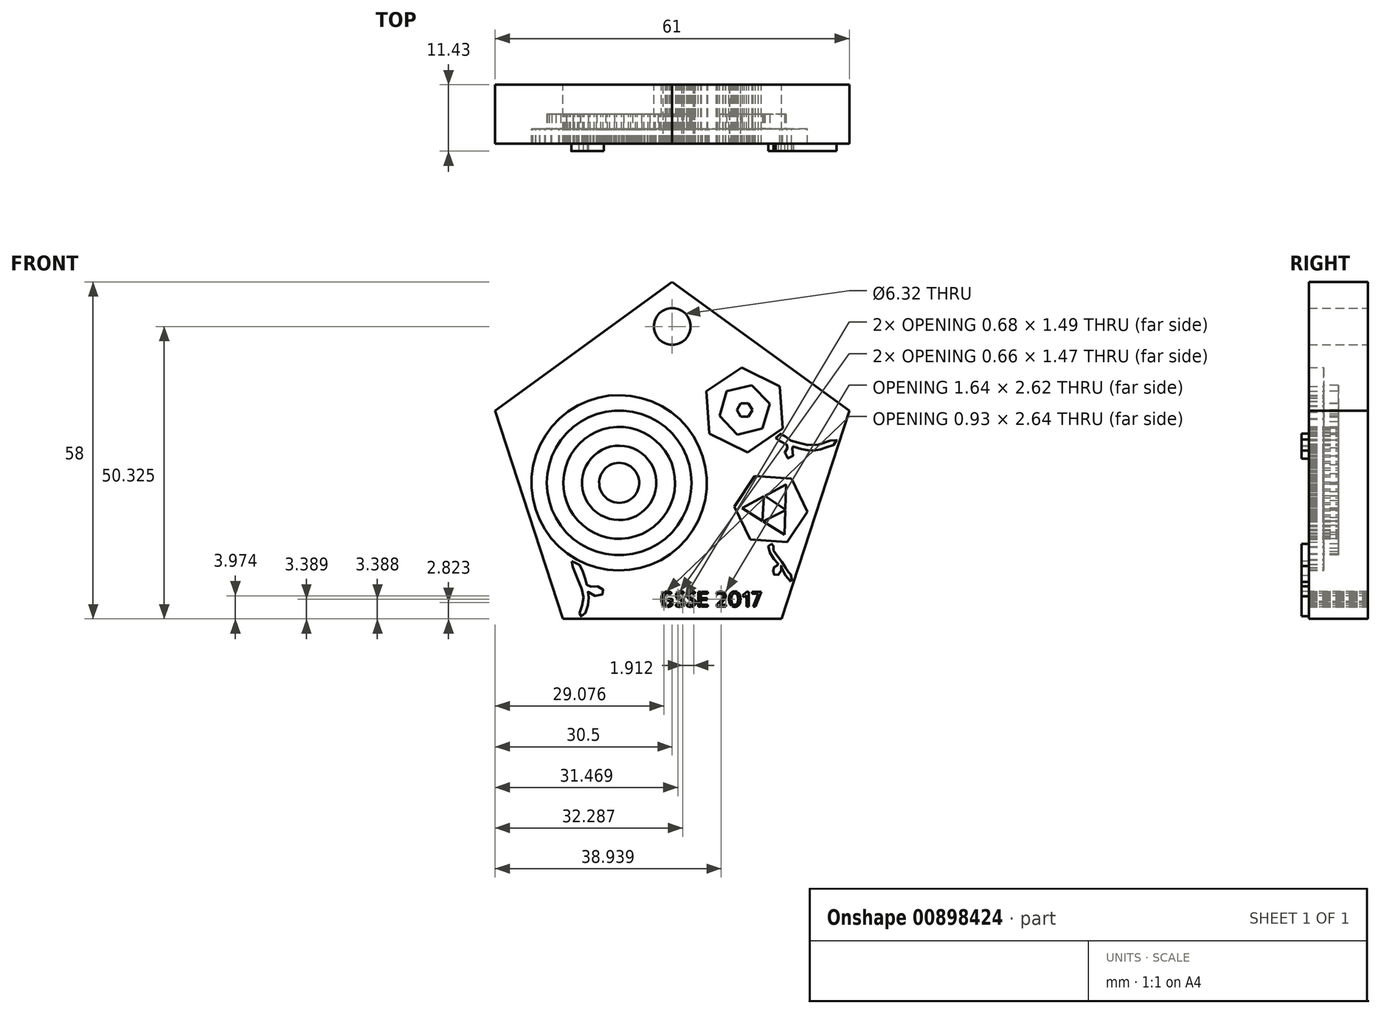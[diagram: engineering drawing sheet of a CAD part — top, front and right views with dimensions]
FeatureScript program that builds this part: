
annotation { "Feature Type Name" : "Feature", "Feature Type Description" : "" }
export const myFeature = defineFeature(function(context is Context, id is Id, definition is map)
    precondition{}
    {
        {
            var Q0;
            Q0=qCreatedBy(makeId("Front.planeOp"),FACE);
            var sketch = newSketch(context, id + "F0", { "sketchPlane" : qUnion([Q0])});
            skCircle(sketch, "E0.cCircle", {"center": v(0, 0) * mm, "radius": 32.06 * mm, "construction": true});
            skLineSegment(sketch, "E0.0", {"start": v(30.5, 9.9) * mm, "end": v(18.85, -25.94) * mm});
            skLineSegment(sketch, "E0.1", {"start": v(18.85, -25.94) * mm, "end": v(-18.85, -25.94) * mm});
            skLineSegment(sketch, "E0.2", {"start": v(-18.85, -25.94) * mm, "end": v(-30.5, 9.9) * mm});
            skLineSegment(sketch, "E0.3", {"start": v(-30.5, 9.9) * mm, "end": v(0, 32.06) * mm});
            skLineSegment(sketch, "E0.4", {"start": v(0, 32.06) * mm, "end": v(30.5, 9.9) * mm});
            skCircle(sketch, "E1", {"center": v(0, 24.38) * mm, "radius": 3.16 * mm});
            skText(sketch, "E2", { "text": "GSSE 2017\n", "fontName": "AllertaStencil-Regular.ttf"});
            const initialGuessF0  = {"E2": [-0.00217, -0.02386, 1, 0, 0.0026]};
            skSetInitialGuess(sketch, initialGuessF0);
            skSolve(sketch);
        }
        {
            var Q0;
            Q0=makeQuery(id+"F0.imprint","IMPRINT",FACE,{"disambiguationData":[TD([[makeQuery(id+"F0.imprint","IMPRINT",EDGE,{"derivedFrom":sQuery(id+"F0.wireOp",EDGE,"E0.0")}),-1.0]])]});
            extrude(context, id + "F1", {"entities" : qUnion([Q0]), "depth" : 7.62 * mm, "offsetDistance" : 25.4 * mm, "symmetric" : true});
        }
        {
            var Q0;
            Q0=makeQuery(id+"F1.opExtrude","CAP_FACE",FACE,{"disambiguationData":[OSD([sQuery(id+"F0.wireOp",EDGE,"E0.0"),sQuery(id+"F0.wireOp",EDGE,"E0.1"),sQuery(id+"F0.wireOp",EDGE,"E0.2"),sQuery(id+"F0.wireOp",EDGE,"E0.3"),sQuery(id+"F0.wireOp",EDGE,"E0.4"),sQuery(id+"F0.wireOp",EDGE,"E1"),sQuery(id+"F0.wireOp",EDGE,"E2.sketch_text.stroke-0"),sQuery(id+"F0.wireOp",EDGE,"E2.sketch_text.stroke-1"),sQuery(id+"F0.wireOp",EDGE,"E2.sketch_text.stroke-2"),sQuery(id+"F0.wireOp",EDGE,"E2.sketch_text.stroke-3"),sQuery(id+"F0.wireOp",EDGE,"E2.sketch_text.stroke-4"),sQuery(id+"F0.wireOp",EDGE,"E2.sketch_text.stroke-5"),sQuery(id+"F0.wireOp",EDGE,"E2.sketch_text.stroke-6"),sQuery(id+"F0.wireOp",EDGE,"E2.sketch_text.stroke-7"),sQuery(id+"F0.wireOp",EDGE,"E2.sketch_text.stroke-8"),sQuery(id+"F0.wireOp",EDGE,"E2.sketch_text.stroke-9"),sQuery(id+"F0.wireOp",EDGE,"E2.sketch_text.stroke-10"),sQuery(id+"F0.wireOp",EDGE,"E2.sketch_text.stroke-11"),sQuery(id+"F0.wireOp",EDGE,"E2.sketch_text.stroke-12"),sQuery(id+"F0.wireOp",EDGE,"E2.sketch_text.stroke-13"),sQuery(id+"F0.wireOp",EDGE,"E2.sketch_text.stroke-14"),sQuery(id+"F0.wireOp",EDGE,"E2.sketch_text.stroke-15"),sQuery(id+"F0.wireOp",EDGE,"E2.sketch_text.stroke-16"),sQuery(id+"F0.wireOp",EDGE,"E2.sketch_text.stroke-17"),sQuery(id+"F0.wireOp",EDGE,"E2.sketch_text.stroke-18"),sQuery(id+"F0.wireOp",EDGE,"E2.sketch_text.stroke-19"),sQuery(id+"F0.wireOp",EDGE,"E2.sketch_text.stroke-20"),sQuery(id+"F0.wireOp",EDGE,"E2.sketch_text.stroke-21"),sQuery(id+"F0.wireOp",EDGE,"E2.sketch_text.stroke-22"),sQuery(id+"F0.wireOp",EDGE,"E2.sketch_text.stroke-23"),sQuery(id+"F0.wireOp",EDGE,"E2.sketch_text.stroke-24"),sQuery(id+"F0.wireOp",EDGE,"E2.sketch_text.stroke-25"),sQuery(id+"F0.wireOp",EDGE,"E2.sketch_text.stroke-26"),sQuery(id+"F0.wireOp",EDGE,"E2.sketch_text.stroke-27"),sQuery(id+"F0.wireOp",EDGE,"E2.sketch_text.stroke-28"),sQuery(id+"F0.wireOp",EDGE,"E2.sketch_text.stroke-29"),sQuery(id+"F0.wireOp",EDGE,"E2.sketch_text.stroke-30"),sQuery(id+"F0.wireOp",EDGE,"E2.sketch_text.stroke-31"),sQuery(id+"F0.wireOp",EDGE,"E2.sketch_text.stroke-32"),sQuery(id+"F0.wireOp",EDGE,"E2.sketch_text.stroke-33"),sQuery(id+"F0.wireOp",EDGE,"E2.sketch_text.stroke-34"),sQuery(id+"F0.wireOp",EDGE,"E2.sketch_text.stroke-35"),sQuery(id+"F0.wireOp",EDGE,"E2.sketch_text.stroke-36"),sQuery(id+"F0.wireOp",EDGE,"E2.sketch_text.stroke-37"),sQuery(id+"F0.wireOp",EDGE,"E2.sketch_text.stroke-38"),sQuery(id+"F0.wireOp",EDGE,"E2.sketch_text.stroke-39"),sQuery(id+"F0.wireOp",EDGE,"E2.sketch_text.stroke-40"),sQuery(id+"F0.wireOp",EDGE,"E2.sketch_text.stroke-41"),sQuery(id+"F0.wireOp",EDGE,"E2.sketch_text.stroke-42"),sQuery(id+"F0.wireOp",EDGE,"E2.sketch_text.stroke-43"),sQuery(id+"F0.wireOp",EDGE,"E2.sketch_text.stroke-44"),sQuery(id+"F0.wireOp",EDGE,"E2.sketch_text.stroke-45"),sQuery(id+"F0.wireOp",EDGE,"E2.sketch_text.stroke-46"),sQuery(id+"F0.wireOp",EDGE,"E2.sketch_text.stroke-47"),sQuery(id+"F0.wireOp",EDGE,"E2.sketch_text.stroke-48"),sQuery(id+"F0.wireOp",EDGE,"E2.sketch_text.stroke-49"),sQuery(id+"F0.wireOp",EDGE,"E2.sketch_text.stroke-50"),sQuery(id+"F0.wireOp",EDGE,"E2.sketch_text.stroke-51"),sQuery(id+"F0.wireOp",EDGE,"E2.sketch_text.stroke-52"),sQuery(id+"F0.wireOp",EDGE,"E2.sketch_text.stroke-53"),sQuery(id+"F0.wireOp",EDGE,"E2.sketch_text.stroke-54"),sQuery(id+"F0.wireOp",EDGE,"E2.sketch_text.stroke-55"),sQuery(id+"F0.wireOp",EDGE,"E2.sketch_text.stroke-56"),sQuery(id+"F0.wireOp",EDGE,"E2.sketch_text.stroke-57"),sQuery(id+"F0.wireOp",EDGE,"E2.sketch_text.stroke-58"),sQuery(id+"F0.wireOp",EDGE,"E2.sketch_text.stroke-59"),sQuery(id+"F0.wireOp",EDGE,"E2.sketch_text.stroke-60"),sQuery(id+"F0.wireOp",EDGE,"E2.sketch_text.stroke-61"),sQuery(id+"F0.wireOp",EDGE,"E2.sketch_text.stroke-62"),sQuery(id+"F0.wireOp",EDGE,"E2.sketch_text.stroke-63"),sQuery(id+"F0.wireOp",EDGE,"E2.sketch_text.stroke-64"),sQuery(id+"F0.wireOp",EDGE,"E2.sketch_text.stroke-65"),sQuery(id+"F0.wireOp",EDGE,"E2.sketch_text.stroke-66"),sQuery(id+"F0.wireOp",EDGE,"E2.sketch_text.stroke-67"),sQuery(id+"F0.wireOp",EDGE,"E2.sketch_text.stroke-68"),sQuery(id+"F0.wireOp",EDGE,"E2.sketch_text.stroke-69"),sQuery(id+"F0.wireOp",EDGE,"E2.sketch_text.stroke-70"),sQuery(id+"F0.wireOp",EDGE,"E2.sketch_text.stroke-71"),sQuery(id+"F0.wireOp",EDGE,"E2.sketch_text.stroke-72"),sQuery(id+"F0.wireOp",EDGE,"E2.sketch_text.stroke-73"),sQuery(id+"F0.wireOp",EDGE,"E2.sketch_text.stroke-74"),sQuery(id+"F0.wireOp",EDGE,"E2.sketch_text.stroke-75"),sQuery(id+"F0.wireOp",EDGE,"E2.sketch_text.stroke-76"),sQuery(id+"F0.wireOp",EDGE,"E2.sketch_text.stroke-77"),sQuery(id+"F0.wireOp",EDGE,"E2.sketch_text.stroke-78"),sQuery(id+"F0.wireOp",EDGE,"E2.sketch_text.stroke-79"),sQuery(id+"F0.wireOp",EDGE,"E2.sketch_text.stroke-80"),sQuery(id+"F0.wireOp",EDGE,"E2.sketch_text.stroke-81"),sQuery(id+"F0.wireOp",EDGE,"E2.sketch_text.stroke-82"),sQuery(id+"F0.wireOp",EDGE,"E2.sketch_text.stroke-83"),sQuery(id+"F0.wireOp",EDGE,"E2.sketch_text.stroke-84"),sQuery(id+"F0.wireOp",EDGE,"E2.sketch_text.stroke-85"),sQuery(id+"F0.wireOp",EDGE,"E2.sketch_text.stroke-86"),sQuery(id+"F0.wireOp",EDGE,"E2.sketch_text.stroke-87"),sQuery(id+"F0.wireOp",EDGE,"E2.sketch_text.stroke-88"),sQuery(id+"F0.wireOp",EDGE,"E2.sketch_text.stroke-89"),sQuery(id+"F0.wireOp",EDGE,"E2.sketch_text.stroke-90"),sQuery(id+"F0.wireOp",EDGE,"E2.sketch_text.stroke-91"),sQuery(id+"F0.wireOp",EDGE,"E2.sketch_text.stroke-92"),sQuery(id+"F0.wireOp",EDGE,"E2.sketch_text.stroke-93"),sQuery(id+"F0.wireOp",EDGE,"E2.sketch_text.stroke-94"),sQuery(id+"F0.wireOp",EDGE,"E2.sketch_text.stroke-95"),sQuery(id+"F0.wireOp",EDGE,"E2.sketch_text.stroke-96"),sQuery(id+"F0.wireOp",EDGE,"E2.sketch_text.stroke-97"),sQuery(id+"F0.wireOp",EDGE,"E2.sketch_text.stroke-98"),sQuery(id+"F0.wireOp",EDGE,"E2.sketch_text.stroke-99"),sQuery(id+"F0.wireOp",EDGE,"E2.sketch_text.stroke-100"),sQuery(id+"F0.wireOp",EDGE,"E2.sketch_text.stroke-101"),sQuery(id+"F0.wireOp",EDGE,"E2.sketch_text.stroke-102"),sQuery(id+"F0.wireOp",EDGE,"E2.sketch_text.stroke-103"),sQuery(id+"F0.wireOp",EDGE,"E2.sketch_text.stroke-104"),sQuery(id+"F0.wireOp",EDGE,"E2.sketch_text.stroke-105"),sQuery(id+"F0.wireOp",EDGE,"E2.sketch_text.stroke-106"),sQuery(id+"F0.wireOp",EDGE,"E2.sketch_text.stroke-107"),sQuery(id+"F0.wireOp",EDGE,"E2.sketch_text.stroke-108"),sQuery(id+"F0.wireOp",EDGE,"E2.sketch_text.stroke-109"),sQuery(id+"F0.wireOp",EDGE,"E2.sketch_text.stroke-110"),sQuery(id+"F0.wireOp",EDGE,"E2.sketch_text.stroke-111"),sQuery(id+"F0.wireOp",EDGE,"E2.sketch_text.stroke-112"),sQuery(id+"F0.wireOp",EDGE,"E2.sketch_text.stroke-113"),sQuery(id+"F0.wireOp",EDGE,"E2.sketch_text.stroke-114"),sQuery(id+"F0.wireOp",EDGE,"E2.sketch_text.stroke-115"),sQuery(id+"F0.wireOp",EDGE,"E2.sketch_text.stroke-116"),sQuery(id+"F0.wireOp",EDGE,"E2.sketch_text.stroke-117"),sQuery(id+"F0.wireOp",EDGE,"E2.sketch_text.stroke-118"),sQuery(id+"F0.wireOp",EDGE,"E2.sketch_text.stroke-119"),sQuery(id+"F0.wireOp",EDGE,"E2.sketch_text.stroke-120"),sQuery(id+"F0.wireOp",EDGE,"E2.sketch_text.stroke-121"),sQuery(id+"F0.wireOp",EDGE,"E2.sketch_text.stroke-122"),sQuery(id+"F0.wireOp",EDGE,"E2.sketch_text.stroke-123"),sQuery(id+"F0.wireOp",EDGE,"E2.sketch_text.stroke-124"),sQuery(id+"F0.wireOp",EDGE,"E2.sketch_text.stroke-125"),sQuery(id+"F0.wireOp",EDGE,"E2.sketch_text.stroke-126"),sQuery(id+"F0.wireOp",EDGE,"E2.sketch_text.stroke-127"),sQuery(id+"F0.wireOp",EDGE,"E2.sketch_text.stroke-128"),sQuery(id+"F0.wireOp",EDGE,"E2.sketch_text.stroke-129"),sQuery(id+"F0.wireOp",EDGE,"E2.sketch_text.stroke-130"),sQuery(id+"F0.wireOp",EDGE,"E2.sketch_text.stroke-131"),sQuery(id+"F0.wireOp",EDGE,"E2.sketch_text.stroke-132"),sQuery(id+"F0.wireOp",EDGE,"E2.sketch_text.stroke-133"),sQuery(id+"F0.wireOp",EDGE,"E2.sketch_text.stroke-134"),sQuery(id+"F0.wireOp",EDGE,"E2.sketch_text.stroke-135"),sQuery(id+"F0.wireOp",EDGE,"E2.sketch_text.stroke-136"),sQuery(id+"F0.wireOp",EDGE,"E2.sketch_text.stroke-137"),sQuery(id+"F0.wireOp",EDGE,"E2.sketch_text.stroke-138"),sQuery(id+"F0.wireOp",EDGE,"E2.sketch_text.stroke-139"),sQuery(id+"F0.wireOp",EDGE,"E2.sketch_text.stroke-140"),sQuery(id+"F0.wireOp",EDGE,"E2.sketch_text.stroke-141"),sQuery(id+"F0.wireOp",EDGE,"E2.sketch_text.stroke-142"),sQuery(id+"F0.wireOp",EDGE,"E2.sketch_text.stroke-143"),sQuery(id+"F0.wireOp",EDGE,"E2.sketch_text.stroke-144"),sQuery(id+"F0.wireOp",EDGE,"E2.sketch_text.stroke-145"),sQuery(id+"F0.wireOp",EDGE,"E2.sketch_text.stroke-146"),sQuery(id+"F0.wireOp",EDGE,"E2.sketch_text.stroke-147"),sQuery(id+"F0.wireOp",EDGE,"E2.sketch_text.stroke-148"),sQuery(id+"F0.wireOp",EDGE,"E2.sketch_text.stroke-149"),sQuery(id+"F0.wireOp",EDGE,"E2.sketch_text.stroke-150"),sQuery(id+"F0.wireOp",EDGE,"E2.sketch_text.stroke-151"),sQuery(id+"F0.wireOp",EDGE,"E2.sketch_text.stroke-152"),sQuery(id+"F0.wireOp",EDGE,"E2.sketch_text.stroke-153"),sQuery(id+"F0.wireOp",EDGE,"E2.sketch_text.stroke-154"),sQuery(id+"F0.wireOp",EDGE,"E2.sketch_text.stroke-155"),sQuery(id+"F0.wireOp",EDGE,"E2.sketch_text.stroke-156"),sQuery(id+"F0.wireOp",EDGE,"E2.sketch_text.stroke-157"),sQuery(id+"F0.wireOp",EDGE,"E2.sketch_text.stroke-158"),sQuery(id+"F0.wireOp",EDGE,"E2.sketch_text.stroke-159"),sQuery(id+"F0.wireOp",EDGE,"E2.sketch_text.stroke-160"),sQuery(id+"F0.wireOp",EDGE,"E2.sketch_text.stroke-161"),sQuery(id+"F0.wireOp",EDGE,"E2.sketch_text.stroke-162"),sQuery(id+"F0.wireOp",EDGE,"E2.sketch_text.stroke-163"),sQuery(id+"F0.wireOp",EDGE,"E2.sketch_text.stroke-164"),sQuery(id+"F0.wireOp",EDGE,"E2.sketch_text.stroke-165"),sQuery(id+"F0.wireOp",EDGE,"E2.sketch_text.stroke-166"),sQuery(id+"F0.wireOp",EDGE,"E2.sketch_text.stroke-167"),sQuery(id+"F0.wireOp",EDGE,"E2.sketch_text.stroke-168"),sQuery(id+"F0.wireOp",EDGE,"E2.sketch_text.stroke-169"),sQuery(id+"F0.wireOp",EDGE,"E2.sketch_text.stroke-170"),sQuery(id+"F0.wireOp",EDGE,"E2.sketch_text.stroke-171"),sQuery(id+"F0.wireOp",EDGE,"E2.sketch_text.stroke-172"),sQuery(id+"F0.wireOp",EDGE,"E2.sketch_text.stroke-173"),sQuery(id+"F0.wireOp",EDGE,"E2.sketch_text.stroke-174"),sQuery(id+"F0.wireOp",EDGE,"E2.sketch_text.stroke-175"),sQuery(id+"F0.wireOp",EDGE,"E2.sketch_text.stroke-176"),sQuery(id+"F0.wireOp",EDGE,"E2.sketch_text.stroke-177"),sQuery(id+"F0.wireOp",EDGE,"E2.sketch_text.stroke-178"),sQuery(id+"F0.wireOp",EDGE,"E2.sketch_text.stroke-179"),sQuery(id+"F0.wireOp",EDGE,"E2.sketch_text.stroke-180"),sQuery(id+"F0.wireOp",EDGE,"E2.sketch_text.stroke-181"),sQuery(id+"F0.wireOp",EDGE,"E2.sketch_text.stroke-182"),sQuery(id+"F0.wireOp",EDGE,"E2.sketch_text.stroke-183"),sQuery(id+"F0.wireOp",EDGE,"E2.sketch_text.stroke-184"),sQuery(id+"F0.wireOp",EDGE,"E2.sketch_text.stroke-185"),sQuery(id+"F0.wireOp",EDGE,"E2.sketch_text.stroke-186"),sQuery(id+"F0.wireOp",EDGE,"E2.sketch_text.stroke-187"),sQuery(id+"F0.wireOp",EDGE,"E2.sketch_text.stroke-188"),sQuery(id+"F0.wireOp",EDGE,"E2.sketch_text.stroke-189"),sQuery(id+"F0.wireOp",EDGE,"E2.sketch_text.stroke-190"),sQuery(id+"F0.wireOp",EDGE,"E2.sketch_text.stroke-191"),sQuery(id+"F0.wireOp",EDGE,"E2.sketch_text.stroke-192"),sQuery(id+"F0.wireOp",EDGE,"E2.sketch_text.stroke-193"),sQuery(id+"F0.wireOp",EDGE,"E2.sketch_text.stroke-194"),sQuery(id+"F0.wireOp",EDGE,"E2.sketch_text.stroke-195"),sQuery(id+"F0.wireOp",EDGE,"E2.sketch_text.stroke-196"),sQuery(id+"F0.wireOp",EDGE,"E2.sketch_text.stroke-197"),sQuery(id+"F0.wireOp",EDGE,"E2.sketch_text.stroke-198"),sQuery(id+"F0.wireOp",EDGE,"E2.sketch_text.stroke-199"),sQuery(id+"F0.wireOp",EDGE,"E2.sketch_text.stroke-200"),sQuery(id+"F0.wireOp",EDGE,"E2.sketch_text.stroke-201"),sQuery(id+"F0.wireOp",EDGE,"E2.sketch_text.stroke-202"),sQuery(id+"F0.wireOp",EDGE,"E2.sketch_text.stroke-203"),sQuery(id+"F0.wireOp",EDGE,"E2.sketch_text.stroke-204"),sQuery(id+"F0.wireOp",EDGE,"E2.sketch_text.stroke-205"),sQuery(id+"F0.wireOp",EDGE,"E2.sketch_text.stroke-206"),sQuery(id+"F0.wireOp",EDGE,"E2.sketch_text.stroke-207"),sQuery(id+"F0.wireOp",EDGE,"E2.sketch_text.stroke-208"),sQuery(id+"F0.wireOp",EDGE,"E2.sketch_text.stroke-209"),sQuery(id+"F0.wireOp",EDGE,"E2.sketch_text.stroke-210"),sQuery(id+"F0.wireOp",EDGE,"E2.sketch_text.stroke-211"),sQuery(id+"F0.wireOp",EDGE,"E2.sketch_text.stroke-212"),sQuery(id+"F0.wireOp",EDGE,"E2.sketch_text.stroke-213"),sQuery(id+"F0.wireOp",EDGE,"E2.sketch_text.stroke-214"),sQuery(id+"F0.wireOp",EDGE,"E2.sketch_text.stroke-215"),sQuery(id+"F0.wireOp",EDGE,"E2.sketch_text.stroke-216"),sQuery(id+"F0.wireOp",EDGE,"E2.sketch_text.stroke-217"),sQuery(id+"F0.wireOp",EDGE,"E2.sketch_text.stroke-218"),sQuery(id+"F0.wireOp",EDGE,"E2.sketch_text.stroke-219"),sQuery(id+"F0.wireOp",EDGE,"E2.sketch_text.stroke-220"),sQuery(id+"F0.wireOp",EDGE,"E2.sketch_text.stroke-221"),sQuery(id+"F0.wireOp",EDGE,"E2.sketch_text.stroke-222"),sQuery(id+"F0.wireOp",EDGE,"E2.sketch_text.stroke-223"),sQuery(id+"F0.wireOp",EDGE,"E2.sketch_text.stroke-224"),sQuery(id+"F0.wireOp",EDGE,"E2.sketch_text.stroke-225"),sQuery(id+"F0.wireOp",EDGE,"E2.sketch_text.stroke-226"),sQuery(id+"F0.wireOp",EDGE,"E2.sketch_text.stroke-227"),sQuery(id+"F0.wireOp",EDGE,"E2.sketch_text.stroke-228"),sQuery(id+"F0.wireOp",EDGE,"E2.sketch_text.stroke-229"),sQuery(id+"F0.wireOp",EDGE,"E2.sketch_text.stroke-230"),sQuery(id+"F0.wireOp",EDGE,"E2.sketch_text.stroke-231"),sQuery(id+"F0.wireOp",EDGE,"E2.sketch_text.stroke-232"),sQuery(id+"F0.wireOp",EDGE,"E2.sketch_text.stroke-233"),sQuery(id+"F0.wireOp",EDGE,"E2.sketch_text.stroke-234"),sQuery(id+"F0.wireOp",EDGE,"E2.sketch_text.stroke-235")])],"isStart":false});
            var sketch = newSketch(context, id + "F2", { "sketchPlane" : qUnion([Q0])});
            skCircle(sketch, "E3.cCircle", {"center": v(-9.13, -2.52) * mm, "radius": 9.62 * mm, "construction": true});
            skLineSegment(sketch, "E3.0", {"start": v(-2.86, 4.77) * mm, "end": v(-2, 3.93) * mm});
            skLineSegment(sketch, "E3.1", {"start": v(-2, 3.93) * mm, "end": v(-1.24, 2.98) * mm});
            skLineSegment(sketch, "E3.2", {"start": v(-1.24, 2.98) * mm, "end": v(-0.61, 1.95) * mm});
            skLineSegment(sketch, "E3.3", {"start": v(-0.61, 1.95) * mm, "end": v(-0.12, 0.85) * mm});
            skLineSegment(sketch, "E3.4", {"start": v(-0.12, 0.85) * mm, "end": v(0.23, -0.3) * mm});
            skLineSegment(sketch, "E3.5", {"start": v(0.23, -0.3) * mm, "end": v(0.44, -1.5) * mm});
            skLineSegment(sketch, "E3.6", {"start": v(0.44, -1.5) * mm, "end": v(0.49, -2.7) * mm});
            skLineSegment(sketch, "E3.7", {"start": v(0.49, -2.7) * mm, "end": v(0.39, -3.91) * mm});
            skLineSegment(sketch, "E3.8", {"start": v(0.39, -3.91) * mm, "end": v(0.14, -5.1) * mm});
            skLineSegment(sketch, "E3.9", {"start": v(0.14, -5.1) * mm, "end": v(-0.26, -6.24) * mm});
            skLineSegment(sketch, "E3.10", {"start": v(-0.26, -6.24) * mm, "end": v(-0.8, -7.32) * mm});
            skLineSegment(sketch, "E3.11", {"start": v(-0.8, -7.32) * mm, "end": v(-1.46, -8.33) * mm});
            skLineSegment(sketch, "E3.12", {"start": v(-1.46, -8.33) * mm, "end": v(-2.25, -9.25) * mm});
            skLineSegment(sketch, "E3.13", {"start": v(-2.25, -9.25) * mm, "end": v(-3.14, -10.06) * mm});
            skLineSegment(sketch, "E3.14", {"start": v(-3.14, -10.06) * mm, "end": v(-4.13, -10.75) * mm});
            skLineSegment(sketch, "E3.15", {"start": v(-4.13, -10.75) * mm, "end": v(-5.2, -11.3) * mm});
            skLineSegment(sketch, "E3.16", {"start": v(-5.2, -11.3) * mm, "end": v(-6.34, -11.73) * mm});
            skLineSegment(sketch, "E3.17", {"start": v(-6.34, -11.73) * mm, "end": v(-7.51, -12.01) * mm});
            skLineSegment(sketch, "E3.18", {"start": v(-7.51, -12.01) * mm, "end": v(-8.71, -12.14) * mm});
            skLineSegment(sketch, "E3.19", {"start": v(-8.71, -12.14) * mm, "end": v(-9.92, -12.12) * mm});
            skLineSegment(sketch, "E3.20", {"start": v(-9.92, -12.12) * mm, "end": v(-11.12, -11.94) * mm});
            skLineSegment(sketch, "E3.21", {"start": v(-11.12, -11.94) * mm, "end": v(-12.28, -11.62) * mm});
            skLineSegment(sketch, "E3.22", {"start": v(-12.28, -11.62) * mm, "end": v(-13.4, -11.15) * mm});
            skLineSegment(sketch, "E3.23", {"start": v(-13.4, -11.15) * mm, "end": v(-14.45, -10.55) * mm});
            skLineSegment(sketch, "E3.24", {"start": v(-14.45, -10.55) * mm, "end": v(-15.41, -9.82) * mm});
            skLineSegment(sketch, "E3.25", {"start": v(-15.41, -9.82) * mm, "end": v(-16.28, -8.98) * mm});
            skLineSegment(sketch, "E3.26", {"start": v(-16.28, -8.98) * mm, "end": v(-17.03, -8.03) * mm});
            skLineSegment(sketch, "E3.27", {"start": v(-17.03, -8.03) * mm, "end": v(-17.66, -7) * mm});
            skLineSegment(sketch, "E3.28", {"start": v(-17.66, -7) * mm, "end": v(-18.15, -5.9) * mm});
            skLineSegment(sketch, "E3.29", {"start": v(-18.15, -5.9) * mm, "end": v(-18.5, -4.74) * mm});
            skLineSegment(sketch, "E3.30", {"start": v(-18.5, -4.74) * mm, "end": v(-18.7, -3.55) * mm});
            skLineSegment(sketch, "E3.31", {"start": v(-18.7, -3.55) * mm, "end": v(-18.76, -2.34) * mm});
            skLineSegment(sketch, "E3.32", {"start": v(-18.76, -2.34) * mm, "end": v(-18.66, -1.14) * mm});
            skLineSegment(sketch, "E3.33", {"start": v(-18.66, -1.14) * mm, "end": v(-18.4, 0.05) * mm});
            skLineSegment(sketch, "E3.34", {"start": v(-18.4, 0.05) * mm, "end": v(-18.01, 1.19) * mm});
            skLineSegment(sketch, "E3.35", {"start": v(-18.01, 1.19) * mm, "end": v(-17.48, 2.27) * mm});
            skLineSegment(sketch, "E3.36", {"start": v(-17.48, 2.27) * mm, "end": v(-16.81, 3.28) * mm});
            skLineSegment(sketch, "E3.37", {"start": v(-16.81, 3.28) * mm, "end": v(-16.02, 4.2) * mm});
            skLineSegment(sketch, "E3.38", {"start": v(-16.02, 4.2) * mm, "end": v(-15.13, 5) * mm});
            skLineSegment(sketch, "E3.39", {"start": v(-15.13, 5) * mm, "end": v(-14.14, 5.7) * mm});
            skLineSegment(sketch, "E3.40", {"start": v(-14.14, 5.7) * mm, "end": v(-13.07, 6.26) * mm});
            skLineSegment(sketch, "E3.41", {"start": v(-13.07, 6.26) * mm, "end": v(-11.93, 6.68) * mm});
            skLineSegment(sketch, "E3.42", {"start": v(-11.93, 6.68) * mm, "end": v(-10.76, 6.96) * mm});
            skLineSegment(sketch, "E3.43", {"start": v(-10.76, 6.96) * mm, "end": v(-9.56, 7.1) * mm});
            skLineSegment(sketch, "E3.44", {"start": v(-9.56, 7.1) * mm, "end": v(-8.35, 7.07) * mm});
            skLineSegment(sketch, "E3.45", {"start": v(-8.35, 7.07) * mm, "end": v(-7.15, 6.9) * mm});
            skLineSegment(sketch, "E3.46", {"start": v(-7.15, 6.9) * mm, "end": v(-5.99, 6.57) * mm});
            skLineSegment(sketch, "E3.47", {"start": v(-5.99, 6.57) * mm, "end": v(-4.87, 6.1) * mm});
            skLineSegment(sketch, "E3.48", {"start": v(-4.87, 6.1) * mm, "end": v(-3.82, 5.5) * mm});
            skLineSegment(sketch, "E3.49", {"start": v(-3.82, 5.5) * mm, "end": v(-2.86, 4.77) * mm});
            skCircle(sketch, "E4.cCircle", {"center": v(-9.13, -2.52) * mm, "radius": 12.46 * mm, "construction": true});
            skLineSegment(sketch, "E4.0", {"start": v(-8.35, 9.9) * mm, "end": v(-6.8, 9.71) * mm});
            skLineSegment(sketch, "E4.1", {"start": v(-6.8, 9.71) * mm, "end": v(-5.28, 9.32) * mm});
            skLineSegment(sketch, "E4.2", {"start": v(-5.28, 9.32) * mm, "end": v(-3.83, 8.75) * mm});
            skLineSegment(sketch, "E4.3", {"start": v(-3.83, 8.75) * mm, "end": v(-2.45, 8) * mm});
            skLineSegment(sketch, "E4.4", {"start": v(-2.45, 8) * mm, "end": v(-1.19, 7.07) * mm});
            skLineSegment(sketch, "E4.5", {"start": v(-1.19, 7.07) * mm, "end": v(-0.05, 6) * mm});
            skLineSegment(sketch, "E4.6", {"start": v(-0.05, 6) * mm, "end": v(0.95, 4.8) * mm});
            skLineSegment(sketch, "E4.7", {"start": v(0.95, 4.8) * mm, "end": v(1.78, 3.47) * mm});
            skLineSegment(sketch, "E4.8", {"start": v(1.78, 3.47) * mm, "end": v(2.45, 2.06) * mm});
            skLineSegment(sketch, "E4.9", {"start": v(2.45, 2.06) * mm, "end": v(2.93, 0.57) * mm});
            skLineSegment(sketch, "E4.10", {"start": v(2.93, 0.57) * mm, "end": v(3.23, -0.97) * mm});
            skLineSegment(sketch, "E4.11", {"start": v(3.23, -0.97) * mm, "end": v(3.32, -2.53) * mm});
            skLineSegment(sketch, "E4.12", {"start": v(3.32, -2.53) * mm, "end": v(3.22, -4.1) * mm});
            skLineSegment(sketch, "E4.13", {"start": v(3.22, -4.1) * mm, "end": v(2.93, -5.63) * mm});
            skLineSegment(sketch, "E4.14", {"start": v(2.93, -5.63) * mm, "end": v(2.45, -7.12) * mm});
            skLineSegment(sketch, "E4.15", {"start": v(2.45, -7.12) * mm, "end": v(1.78, -8.53) * mm});
            skLineSegment(sketch, "E4.16", {"start": v(1.78, -8.53) * mm, "end": v(0.94, -9.85) * mm});
            skLineSegment(sketch, "E4.17", {"start": v(0.94, -9.85) * mm, "end": v(-0.06, -11.06) * mm});
            skLineSegment(sketch, "E4.18", {"start": v(-0.06, -11.06) * mm, "end": v(-1.2, -12.13) * mm});
            skLineSegment(sketch, "E4.19", {"start": v(-1.2, -12.13) * mm, "end": v(-2.46, -13.05) * mm});
            skLineSegment(sketch, "E4.20", {"start": v(-2.46, -13.05) * mm, "end": v(-3.84, -13.8) * mm});
            skLineSegment(sketch, "E4.21", {"start": v(-3.84, -13.8) * mm, "end": v(-5.3, -14.37) * mm});
            skLineSegment(sketch, "E4.22", {"start": v(-5.3, -14.37) * mm, "end": v(-6.8, -14.76) * mm});
            skLineSegment(sketch, "E4.23", {"start": v(-6.8, -14.76) * mm, "end": v(-8.36, -14.96) * mm});
            skLineSegment(sketch, "E4.24", {"start": v(-8.36, -14.96) * mm, "end": v(-9.92, -14.96) * mm});
            skLineSegment(sketch, "E4.25", {"start": v(-9.92, -14.96) * mm, "end": v(-11.47, -14.76) * mm});
            skLineSegment(sketch, "E4.26", {"start": v(-11.47, -14.76) * mm, "end": v(-12.99, -14.37) * mm});
            skLineSegment(sketch, "E4.27", {"start": v(-12.99, -14.37) * mm, "end": v(-14.44, -13.8) * mm});
            skLineSegment(sketch, "E4.28", {"start": v(-14.44, -13.8) * mm, "end": v(-15.81, -13.04) * mm});
            skLineSegment(sketch, "E4.29", {"start": v(-15.81, -13.04) * mm, "end": v(-17.08, -12.12) * mm});
            skLineSegment(sketch, "E4.30", {"start": v(-17.08, -12.12) * mm, "end": v(-18.22, -11.05) * mm});
            skLineSegment(sketch, "E4.31", {"start": v(-18.22, -11.05) * mm, "end": v(-19.22, -9.84) * mm});
            skLineSegment(sketch, "E4.32", {"start": v(-19.22, -9.84) * mm, "end": v(-20.05, -8.52) * mm});
            skLineSegment(sketch, "E4.33", {"start": v(-20.05, -8.52) * mm, "end": v(-20.72, -7.1) * mm});
            skLineSegment(sketch, "E4.34", {"start": v(-20.72, -7.1) * mm, "end": v(-21.2, -5.62) * mm});
            skLineSegment(sketch, "E4.35", {"start": v(-21.2, -5.62) * mm, "end": v(-21.5, -4.08) * mm});
            skLineSegment(sketch, "E4.36", {"start": v(-21.5, -4.08) * mm, "end": v(-21.6, -2.52) * mm});
            skLineSegment(sketch, "E4.37", {"start": v(-21.6, -2.52) * mm, "end": v(-21.5, -0.96) * mm});
            skLineSegment(sketch, "E4.38", {"start": v(-21.5, -0.96) * mm, "end": v(-21.2, 0.58) * mm});
            skLineSegment(sketch, "E4.39", {"start": v(-21.2, 0.58) * mm, "end": v(-20.72, 2.07) * mm});
            skLineSegment(sketch, "E4.40", {"start": v(-20.72, 2.07) * mm, "end": v(-20.05, 3.48) * mm});
            skLineSegment(sketch, "E4.41", {"start": v(-20.05, 3.48) * mm, "end": v(-19.2, 4.8) * mm});
            skLineSegment(sketch, "E4.42", {"start": v(-19.2, 4.8) * mm, "end": v(-18.21, 6) * mm});
            skLineSegment(sketch, "E4.43", {"start": v(-18.21, 6) * mm, "end": v(-17.07, 7.08) * mm});
            skLineSegment(sketch, "E4.44", {"start": v(-17.07, 7.08) * mm, "end": v(-15.8, 8) * mm});
            skLineSegment(sketch, "E4.45", {"start": v(-15.8, 8) * mm, "end": v(-14.43, 8.75) * mm});
            skLineSegment(sketch, "E4.46", {"start": v(-14.43, 8.75) * mm, "end": v(-12.98, 9.33) * mm});
            skLineSegment(sketch, "E4.47", {"start": v(-12.98, 9.33) * mm, "end": v(-11.46, 9.71) * mm});
            skLineSegment(sketch, "E4.48", {"start": v(-11.46, 9.71) * mm, "end": v(-9.91, 9.9) * mm});
            skLineSegment(sketch, "E4.49", {"start": v(-9.91, 9.9) * mm, "end": v(-8.35, 9.9) * mm});
            skCircle(sketch, "E5.cCircle", {"center": v(-9.13, -2.52) * mm, "radius": 15.1 * mm, "construction": true});
            skLineSegment(sketch, "E5.0", {"start": v(-5.28, 12.07) * mm, "end": v(-3.48, 11.47) * mm});
            skLineSegment(sketch, "E5.1", {"start": v(-3.48, 11.47) * mm, "end": v(-1.77, 10.65) * mm});
            skLineSegment(sketch, "E5.2", {"start": v(-1.77, 10.65) * mm, "end": v(-0.18, 9.63) * mm});
            skLineSegment(sketch, "E5.3", {"start": v(-0.18, 9.63) * mm, "end": v(1.27, 8.4) * mm});
            skLineSegment(sketch, "E5.4", {"start": v(1.27, 8.4) * mm, "end": v(2.56, 7.02) * mm});
            skLineSegment(sketch, "E5.5", {"start": v(2.56, 7.02) * mm, "end": v(3.67, 5.48) * mm});
            skLineSegment(sketch, "E5.6", {"start": v(3.67, 5.48) * mm, "end": v(4.57, 3.8) * mm});
            skLineSegment(sketch, "E5.7", {"start": v(4.57, 3.8) * mm, "end": v(5.25, 2.04) * mm});
            skLineSegment(sketch, "E5.8", {"start": v(5.25, 2.04) * mm, "end": v(5.71, 0.2) * mm});
            skLineSegment(sketch, "E5.9", {"start": v(5.71, 0.2) * mm, "end": v(5.94, -1.68) * mm});
            skLineSegment(sketch, "E5.10", {"start": v(5.94, -1.68) * mm, "end": v(5.92, -3.58) * mm});
            skLineSegment(sketch, "E5.11", {"start": v(5.92, -3.58) * mm, "end": v(5.67, -5.46) * mm});
            skLineSegment(sketch, "E5.12", {"start": v(5.67, -5.46) * mm, "end": v(5.19, -7.29) * mm});
            skLineSegment(sketch, "E5.13", {"start": v(5.19, -7.29) * mm, "end": v(4.48, -9.05) * mm});
            skLineSegment(sketch, "E5.14", {"start": v(4.48, -9.05) * mm, "end": v(3.55, -10.7) * mm});
            skLineSegment(sketch, "E5.15", {"start": v(3.55, -10.7) * mm, "end": v(2.43, -12.23) * mm});
            skLineSegment(sketch, "E5.16", {"start": v(2.43, -12.23) * mm, "end": v(1.12, -13.6) * mm});
            skLineSegment(sketch, "E5.17", {"start": v(1.12, -13.6) * mm, "end": v(-0.35, -14.8) * mm});
            skLineSegment(sketch, "E5.18", {"start": v(-0.35, -14.8) * mm, "end": v(-1.95, -15.8) * mm});
            skLineSegment(sketch, "E5.19", {"start": v(-1.95, -15.8) * mm, "end": v(-3.68, -16.6) * mm});
            skLineSegment(sketch, "E5.20", {"start": v(-3.68, -16.6) * mm, "end": v(-5.48, -17.17) * mm});
            skLineSegment(sketch, "E5.21", {"start": v(-5.48, -17.17) * mm, "end": v(-7.35, -17.51) * mm});
            skLineSegment(sketch, "E5.22", {"start": v(-7.35, -17.51) * mm, "end": v(-9.24, -17.62) * mm});
            skLineSegment(sketch, "E5.23", {"start": v(-9.24, -17.62) * mm, "end": v(-11.13, -17.49) * mm});
            skLineSegment(sketch, "E5.24", {"start": v(-11.13, -17.49) * mm, "end": v(-12.99, -17.12) * mm});
            skLineSegment(sketch, "E5.25", {"start": v(-12.99, -17.12) * mm, "end": v(-14.79, -16.52) * mm});
            skLineSegment(sketch, "E5.26", {"start": v(-14.79, -16.52) * mm, "end": v(-16.5, -15.7) * mm});
            skLineSegment(sketch, "E5.27", {"start": v(-16.5, -15.7) * mm, "end": v(-18.1, -14.67) * mm});
            skLineSegment(sketch, "E5.28", {"start": v(-18.1, -14.67) * mm, "end": v(-19.54, -13.46) * mm});
            skLineSegment(sketch, "E5.29", {"start": v(-19.54, -13.46) * mm, "end": v(-20.83, -12.07) * mm});
            skLineSegment(sketch, "E5.30", {"start": v(-20.83, -12.07) * mm, "end": v(-21.94, -10.52) * mm});
            skLineSegment(sketch, "E5.31", {"start": v(-21.94, -10.52) * mm, "end": v(-22.84, -8.86) * mm});
            skLineSegment(sketch, "E5.32", {"start": v(-22.84, -8.86) * mm, "end": v(-23.52, -7.09) * mm});
            skLineSegment(sketch, "E5.33", {"start": v(-23.52, -7.09) * mm, "end": v(-23.98, -5.25) * mm});
            skLineSegment(sketch, "E5.34", {"start": v(-23.98, -5.25) * mm, "end": v(-24.2, -3.37) * mm});
            skLineSegment(sketch, "E5.35", {"start": v(-24.2, -3.37) * mm, "end": v(-24.2, -1.47) * mm});
            skLineSegment(sketch, "E5.36", {"start": v(-24.2, -1.47) * mm, "end": v(-23.94, 0.4) * mm});
            skLineSegment(sketch, "E5.37", {"start": v(-23.94, 0.4) * mm, "end": v(-23.46, 2.24) * mm});
            skLineSegment(sketch, "E5.38", {"start": v(-23.46, 2.24) * mm, "end": v(-22.75, 4) * mm});
            skLineSegment(sketch, "E5.39", {"start": v(-22.75, 4) * mm, "end": v(-21.82, 5.65) * mm});
            skLineSegment(sketch, "E5.40", {"start": v(-21.82, 5.65) * mm, "end": v(-20.7, 7.18) * mm});
            skLineSegment(sketch, "E5.41", {"start": v(-20.7, 7.18) * mm, "end": v(-19.4, 8.55) * mm});
            skLineSegment(sketch, "E5.42", {"start": v(-19.4, 8.55) * mm, "end": v(-17.92, 9.75) * mm});
            skLineSegment(sketch, "E5.43", {"start": v(-17.92, 9.75) * mm, "end": v(-16.32, 10.75) * mm});
            skLineSegment(sketch, "E5.44", {"start": v(-16.32, 10.75) * mm, "end": v(-14.6, 11.55) * mm});
            skLineSegment(sketch, "E5.45", {"start": v(-14.6, 11.55) * mm, "end": v(-12.79, 12.12) * mm});
            skLineSegment(sketch, "E5.46", {"start": v(-12.79, 12.12) * mm, "end": v(-10.92, 12.46) * mm});
            skLineSegment(sketch, "E5.47", {"start": v(-10.92, 12.46) * mm, "end": v(-9.03, 12.57) * mm});
            skLineSegment(sketch, "E5.48", {"start": v(-9.03, 12.57) * mm, "end": v(-7.14, 12.44) * mm});
            skLineSegment(sketch, "E5.49", {"start": v(-7.14, 12.44) * mm, "end": v(-5.28, 12.07) * mm});
            skCircle(sketch, "E6.cCircle", {"center": v(-9.13, -2.52) * mm, "radius": 6.4 * mm, "construction": true});
            skLineSegment(sketch, "E6.0", {"start": v(-5.28, 2.58) * mm, "end": v(-4.67, 2.06) * mm});
            skLineSegment(sketch, "E6.1", {"start": v(-4.67, 2.06) * mm, "end": v(-4.13, 1.46) * mm});
            skLineSegment(sketch, "E6.2", {"start": v(-4.13, 1.46) * mm, "end": v(-3.67, 0.8) * mm});
            skLineSegment(sketch, "E6.3", {"start": v(-3.67, 0.8) * mm, "end": v(-3.3, 0.1) * mm});
            skLineSegment(sketch, "E6.4", {"start": v(-3.3, 0.1) * mm, "end": v(-3.01, -0.66) * mm});
            skLineSegment(sketch, "E6.5", {"start": v(-3.01, -0.66) * mm, "end": v(-2.83, -1.44) * mm});
            skLineSegment(sketch, "E6.6", {"start": v(-2.83, -1.44) * mm, "end": v(-2.74, -2.24) * mm});
            skLineSegment(sketch, "E6.7", {"start": v(-2.74, -2.24) * mm, "end": v(-2.76, -3.04) * mm});
            skLineSegment(sketch, "E6.8", {"start": v(-2.76, -3.04) * mm, "end": v(-2.87, -3.84) * mm});
            skLineSegment(sketch, "E6.9", {"start": v(-2.87, -3.84) * mm, "end": v(-3.09, -4.61) * mm});
            skLineSegment(sketch, "E6.10", {"start": v(-3.09, -4.61) * mm, "end": v(-3.4, -5.35) * mm});
            skLineSegment(sketch, "E6.11", {"start": v(-3.4, -5.35) * mm, "end": v(-3.8, -6.05) * mm});
            skLineSegment(sketch, "E6.12", {"start": v(-3.8, -6.05) * mm, "end": v(-4.28, -6.7) * mm});
            skLineSegment(sketch, "E6.13", {"start": v(-4.28, -6.7) * mm, "end": v(-4.84, -7.27) * mm});
            skLineSegment(sketch, "E6.14", {"start": v(-4.84, -7.27) * mm, "end": v(-5.47, -7.77) * mm});
            skLineSegment(sketch, "E6.15", {"start": v(-5.47, -7.77) * mm, "end": v(-6.15, -8.19) * mm});
            skLineSegment(sketch, "E6.16", {"start": v(-6.15, -8.19) * mm, "end": v(-6.89, -8.52) * mm});
            skLineSegment(sketch, "E6.17", {"start": v(-6.89, -8.52) * mm, "end": v(-7.66, -8.75) * mm});
            skLineSegment(sketch, "E6.18", {"start": v(-7.66, -8.75) * mm, "end": v(-8.45, -8.89) * mm});
            skLineSegment(sketch, "E6.19", {"start": v(-8.45, -8.89) * mm, "end": v(-9.25, -8.92) * mm});
            skLineSegment(sketch, "E6.20", {"start": v(-9.25, -8.92) * mm, "end": v(-10.05, -8.86) * mm});
            skLineSegment(sketch, "E6.21", {"start": v(-10.05, -8.86) * mm, "end": v(-10.84, -8.7) * mm});
            skLineSegment(sketch, "E6.22", {"start": v(-10.84, -8.7) * mm, "end": v(-11.6, -8.43) * mm});
            skLineSegment(sketch, "E6.23", {"start": v(-11.6, -8.43) * mm, "end": v(-12.32, -8.07) * mm});
            skLineSegment(sketch, "E6.24", {"start": v(-12.32, -8.07) * mm, "end": v(-12.99, -7.63) * mm});
            skLineSegment(sketch, "E6.25", {"start": v(-12.99, -7.63) * mm, "end": v(-13.6, -7.1) * mm});
            skLineSegment(sketch, "E6.26", {"start": v(-13.6, -7.1) * mm, "end": v(-14.14, -6.51) * mm});
            skLineSegment(sketch, "E6.27", {"start": v(-14.14, -6.51) * mm, "end": v(-14.6, -5.85) * mm});
            skLineSegment(sketch, "E6.28", {"start": v(-14.6, -5.85) * mm, "end": v(-14.97, -5.14) * mm});
            skLineSegment(sketch, "E6.29", {"start": v(-14.97, -5.14) * mm, "end": v(-15.26, -4.4) * mm});
            skLineSegment(sketch, "E6.30", {"start": v(-15.26, -4.4) * mm, "end": v(-15.44, -3.6) * mm});
            skLineSegment(sketch, "E6.31", {"start": v(-15.44, -3.6) * mm, "end": v(-15.53, -2.8) * mm});
            skLineSegment(sketch, "E6.32", {"start": v(-15.53, -2.8) * mm, "end": v(-15.51, -2) * mm});
            skLineSegment(sketch, "E6.33", {"start": v(-15.51, -2) * mm, "end": v(-15.4, -1.21) * mm});
            skLineSegment(sketch, "E6.34", {"start": v(-15.4, -1.21) * mm, "end": v(-15.18, -0.44) * mm});
            skLineSegment(sketch, "E6.35", {"start": v(-15.18, -0.44) * mm, "end": v(-14.87, 0.3) * mm});
            skLineSegment(sketch, "E6.36", {"start": v(-14.87, 0.3) * mm, "end": v(-14.47, 1) * mm});
            skLineSegment(sketch, "E6.37", {"start": v(-14.47, 1) * mm, "end": v(-14, 1.64) * mm});
            skLineSegment(sketch, "E6.38", {"start": v(-14, 1.64) * mm, "end": v(-13.43, 2.22) * mm});
            skLineSegment(sketch, "E6.39", {"start": v(-13.43, 2.22) * mm, "end": v(-12.8, 2.72) * mm});
            skLineSegment(sketch, "E6.40", {"start": v(-12.8, 2.72) * mm, "end": v(-12.12, 3.14) * mm});
            skLineSegment(sketch, "E6.41", {"start": v(-12.12, 3.14) * mm, "end": v(-11.38, 3.47) * mm});
            skLineSegment(sketch, "E6.42", {"start": v(-11.38, 3.47) * mm, "end": v(-10.61, 3.7) * mm});
            skLineSegment(sketch, "E6.43", {"start": v(-10.61, 3.7) * mm, "end": v(-9.82, 3.84) * mm});
            skLineSegment(sketch, "E6.44", {"start": v(-9.82, 3.84) * mm, "end": v(-9.02, 3.87) * mm});
            skLineSegment(sketch, "E6.45", {"start": v(-9.02, 3.87) * mm, "end": v(-8.22, 3.8) * mm});
            skLineSegment(sketch, "E6.46", {"start": v(-8.22, 3.8) * mm, "end": v(-7.43, 3.64) * mm});
            skLineSegment(sketch, "E6.47", {"start": v(-7.43, 3.64) * mm, "end": v(-6.67, 3.38) * mm});
            skLineSegment(sketch, "E6.48", {"start": v(-6.67, 3.38) * mm, "end": v(-5.95, 3.03) * mm});
            skLineSegment(sketch, "E6.49", {"start": v(-5.95, 3.03) * mm, "end": v(-5.28, 2.58) * mm});
            skCircle(sketch, "E7.cCircle", {"center": v(-9.13, -2.52) * mm, "radius": 3.44 * mm, "construction": true});
            skLineSegment(sketch, "E7.0", {"start": v(-6.8, 0) * mm, "end": v(-6.5, -0.31) * mm});
            skLineSegment(sketch, "E7.1", {"start": v(-6.5, -0.31) * mm, "end": v(-6.24, -0.66) * mm});
            skLineSegment(sketch, "E7.2", {"start": v(-6.24, -0.66) * mm, "end": v(-6.03, -1.04) * mm});
            skLineSegment(sketch, "E7.3", {"start": v(-6.03, -1.04) * mm, "end": v(-5.87, -1.44) * mm});
            skLineSegment(sketch, "E7.4", {"start": v(-5.87, -1.44) * mm, "end": v(-5.76, -1.86) * mm});
            skLineSegment(sketch, "E7.5", {"start": v(-5.76, -1.86) * mm, "end": v(-5.7, -2.29) * mm});
            skLineSegment(sketch, "E7.6", {"start": v(-5.7, -2.29) * mm, "end": v(-5.7, -2.72) * mm});
            skLineSegment(sketch, "E7.7", {"start": v(-5.7, -2.72) * mm, "end": v(-5.75, -3.15) * mm});
            skLineSegment(sketch, "E7.8", {"start": v(-5.75, -3.15) * mm, "end": v(-5.85, -3.57) * mm});
            skLineSegment(sketch, "E7.9", {"start": v(-5.85, -3.57) * mm, "end": v(-6.01, -3.97) * mm});
            skLineSegment(sketch, "E7.10", {"start": v(-6.01, -3.97) * mm, "end": v(-6.22, -4.35) * mm});
            skLineSegment(sketch, "E7.11", {"start": v(-6.22, -4.35) * mm, "end": v(-6.47, -4.7) * mm});
            skLineSegment(sketch, "E7.12", {"start": v(-6.47, -4.7) * mm, "end": v(-6.76, -5.02) * mm});
            skLineSegment(sketch, "E7.13", {"start": v(-6.76, -5.02) * mm, "end": v(-7.1, -5.3) * mm});
            skLineSegment(sketch, "E7.14", {"start": v(-7.1, -5.3) * mm, "end": v(-7.46, -5.53) * mm});
            skLineSegment(sketch, "E7.15", {"start": v(-7.46, -5.53) * mm, "end": v(-7.85, -5.72) * mm});
            skLineSegment(sketch, "E7.16", {"start": v(-7.85, -5.72) * mm, "end": v(-8.26, -5.85) * mm});
            skLineSegment(sketch, "E7.17", {"start": v(-8.26, -5.85) * mm, "end": v(-8.68, -5.94) * mm});
            skLineSegment(sketch, "E7.18", {"start": v(-8.68, -5.94) * mm, "end": v(-9.11, -5.97) * mm});
            skLineSegment(sketch, "E7.19", {"start": v(-9.11, -5.97) * mm, "end": v(-9.54, -5.94) * mm});
            skLineSegment(sketch, "E7.20", {"start": v(-9.54, -5.94) * mm, "end": v(-9.97, -5.86) * mm});
            skLineSegment(sketch, "E7.21", {"start": v(-9.97, -5.86) * mm, "end": v(-10.38, -5.73) * mm});
            skLineSegment(sketch, "E7.22", {"start": v(-10.38, -5.73) * mm, "end": v(-10.77, -5.55) * mm});
            skLineSegment(sketch, "E7.23", {"start": v(-10.77, -5.55) * mm, "end": v(-11.14, -5.32) * mm});
            skLineSegment(sketch, "E7.24", {"start": v(-11.14, -5.32) * mm, "end": v(-11.47, -5.05) * mm});
            skLineSegment(sketch, "E7.25", {"start": v(-11.47, -5.05) * mm, "end": v(-11.77, -4.73) * mm});
            skLineSegment(sketch, "E7.26", {"start": v(-11.77, -4.73) * mm, "end": v(-12.03, -4.39) * mm});
            skLineSegment(sketch, "E7.27", {"start": v(-12.03, -4.39) * mm, "end": v(-12.24, -4) * mm});
            skLineSegment(sketch, "E7.28", {"start": v(-12.24, -4) * mm, "end": v(-12.4, -3.6) * mm});
            skLineSegment(sketch, "E7.29", {"start": v(-12.4, -3.6) * mm, "end": v(-12.51, -3.2) * mm});
            skLineSegment(sketch, "E7.30", {"start": v(-12.51, -3.2) * mm, "end": v(-12.57, -2.76) * mm});
            skLineSegment(sketch, "E7.31", {"start": v(-12.57, -2.76) * mm, "end": v(-12.57, -2.33) * mm});
            skLineSegment(sketch, "E7.32", {"start": v(-12.57, -2.33) * mm, "end": v(-12.52, -1.9) * mm});
            skLineSegment(sketch, "E7.33", {"start": v(-12.52, -1.9) * mm, "end": v(-12.41, -1.48) * mm});
            skLineSegment(sketch, "E7.34", {"start": v(-12.41, -1.48) * mm, "end": v(-12.26, -1.08) * mm});
            skLineSegment(sketch, "E7.35", {"start": v(-12.26, -1.08) * mm, "end": v(-12.05, -0.7) * mm});
            skLineSegment(sketch, "E7.36", {"start": v(-12.05, -0.7) * mm, "end": v(-11.8, -0.35) * mm});
            skLineSegment(sketch, "E7.37", {"start": v(-11.8, -0.35) * mm, "end": v(-11.5, -0.03) * mm});
            skLineSegment(sketch, "E7.38", {"start": v(-11.5, -0.03) * mm, "end": v(-11.18, 0.25) * mm});
            skLineSegment(sketch, "E7.39", {"start": v(-11.18, 0.25) * mm, "end": v(-10.81, 0.48) * mm});
            skLineSegment(sketch, "E7.40", {"start": v(-10.81, 0.48) * mm, "end": v(-10.42, 0.67) * mm});
            skLineSegment(sketch, "E7.41", {"start": v(-10.42, 0.67) * mm, "end": v(-10.01, 0.8) * mm});
            skLineSegment(sketch, "E7.42", {"start": v(-10.01, 0.8) * mm, "end": v(-9.59, 0.89) * mm});
            skLineSegment(sketch, "E7.43", {"start": v(-9.59, 0.89) * mm, "end": v(-9.16, 0.92) * mm});
            skLineSegment(sketch, "E7.44", {"start": v(-9.16, 0.92) * mm, "end": v(-8.73, 0.9) * mm});
            skLineSegment(sketch, "E7.45", {"start": v(-8.73, 0.9) * mm, "end": v(-8.3, 0.82) * mm});
            skLineSegment(sketch, "E7.46", {"start": v(-8.3, 0.82) * mm, "end": v(-7.89, 0.68) * mm});
            skLineSegment(sketch, "E7.47", {"start": v(-7.89, 0.68) * mm, "end": v(-7.5, 0.5) * mm});
            skLineSegment(sketch, "E7.48", {"start": v(-7.5, 0.5) * mm, "end": v(-7.13, 0.27) * mm});
            skLineSegment(sketch, "E7.49", {"start": v(-7.13, 0.27) * mm, "end": v(-6.8, 0) * mm});
            skLineSegment(sketch, "E8.0", {"start": v(15.53, 6.82) * mm, "end": v(11.22, 5.77) * mm});
            skLineSegment(sketch, "E8.1", {"start": v(11.22, 5.77) * mm, "end": v(8.15, 8.98) * mm});
            skLineSegment(sketch, "E8.2", {"start": v(8.15, 8.98) * mm, "end": v(9.4, 13.24) * mm});
            skLineSegment(sketch, "E8.3", {"start": v(9.4, 13.24) * mm, "end": v(13.71, 14.29) * mm});
            skLineSegment(sketch, "E8.4", {"start": v(13.71, 14.29) * mm, "end": v(16.78, 11.08) * mm});
            skLineSegment(sketch, "E8.5", {"start": v(16.78, 11.08) * mm, "end": v(15.53, 6.82) * mm});
            skLineSegment(sketch, "E9.0", {"start": v(19.03, 6.82) * mm, "end": v(12.97, 2.73) * mm});
            skLineSegment(sketch, "E9.1", {"start": v(12.97, 2.73) * mm, "end": v(6.4, 5.94) * mm});
            skLineSegment(sketch, "E9.2", {"start": v(6.4, 5.94) * mm, "end": v(5.9, 13.24) * mm});
            skLineSegment(sketch, "E9.3", {"start": v(5.9, 13.24) * mm, "end": v(11.96, 17.32) * mm});
            skLineSegment(sketch, "E9.4", {"start": v(11.96, 17.32) * mm, "end": v(18.53, 14.1) * mm});
            skLineSegment(sketch, "E9.5", {"start": v(18.53, 14.1) * mm, "end": v(19.03, 6.82) * mm});
            skLineSegment(sketch, "E10.0", {"start": v(15.53, -9.24) * mm, "end": v(15.82, -4.69) * mm});
            skLineSegment(sketch, "E10.1", {"start": v(15.82, -4.69) * mm, "end": v(19.61, -7.22) * mm});
            skLineSegment(sketch, "E10.2", {"start": v(19.61, -7.22) * mm, "end": v(15.53, -9.24) * mm});
            skArc(sketch, "E11.trimOffspring", {"start": v(12.84, 2.8) * mm, "mid": v(12.75, 2.76) * mm, "end": v(12.66, 2.72) * mm, "construction": true});
            skArc(sketch, "E12.trimOffspring", {"start": v(12.66, 2.72) * mm, "mid": v(12.82, 2.73) * mm, "end": v(12.97, 2.73) * mm, "construction": true});
            skLineSegment(sketch, "E13.0", {"start": v(19.61, -2.82) * mm, "end": v(19.34, -11.44) * mm});
            skLineSegment(sketch, "E13.1", {"start": v(19.34, -11.44) * mm, "end": v(12.01, -6.9) * mm});
            skLineSegment(sketch, "E13.2", {"start": v(12.01, -6.9) * mm, "end": v(19.61, -2.82) * mm});
            skLineSegment(sketch, "E14.0", {"start": v(14.22, -1.36) * mm, "end": v(20.53, -1.8) * mm});
            skLineSegment(sketch, "E14.1", {"start": v(20.53, -1.8) * mm, "end": v(23.3, -7.5) * mm});
            skLineSegment(sketch, "E14.2", {"start": v(23.3, -7.5) * mm, "end": v(19.76, -12.74) * mm});
            skLineSegment(sketch, "E14.3", {"start": v(19.76, -12.74) * mm, "end": v(13.45, -12.3) * mm});
            skLineSegment(sketch, "E14.4", {"start": v(13.45, -12.3) * mm, "end": v(10.67, -6.6) * mm});
            skLineSegment(sketch, "E14.5", {"start": v(10.67, -6.6) * mm, "end": v(14.22, -1.36) * mm});
            skCircle(sketch, "E15.cCircle", {"center": v(12.46, 10.03) * mm, "radius": 1.33 * mm, "construction": true});
            skLineSegment(sketch, "E15.0", {"start": v(13.8, 10.03) * mm, "end": v(13.13, 8.87) * mm});
            skLineSegment(sketch, "E15.1", {"start": v(13.13, 8.87) * mm, "end": v(11.8, 8.87) * mm});
            skLineSegment(sketch, "E15.2", {"start": v(11.8, 8.87) * mm, "end": v(11.13, 10.03) * mm});
            skLineSegment(sketch, "E15.3", {"start": v(11.13, 10.03) * mm, "end": v(11.8, 11.18) * mm});
            skLineSegment(sketch, "E15.4", {"start": v(11.8, 11.18) * mm, "end": v(13.13, 11.18) * mm});
            skLineSegment(sketch, "E15.5", {"start": v(13.13, 11.18) * mm, "end": v(13.8, 10.03) * mm});
            skSolve(sketch);
        }
        {
            var Q0;
            Q0=makeQuery(id+"F2.imprint","IMPRINT",FACE,{"disambiguationData":[TD([[makeQuery(id+"F2.imprint","IMPRINT",EDGE,{"derivedFrom":sQuery(id+"F2.wireOp",EDGE,"E5.0")}),1.0]])]});
            var Q1;
            Q1=makeQuery(id+"F2.imprint","IMPRINT",FACE,{"disambiguationData":[TD([[makeQuery(id+"F2.imprint","IMPRINT",EDGE,{"derivedFrom":sQuery(id+"F2.wireOp",EDGE,"E3.0")}),-1.0]])]});
            var Q2;
            Q2=makeQuery(id+"F2.imprint","IMPRINT",FACE,{"disambiguationData":[TD([[makeQuery(id+"F2.imprint","IMPRINT",EDGE,{"derivedFrom":sQuery(id+"F2.wireOp",EDGE,"E7.0")}),-1.0]])]});
            extrude(context, id + "F3", {"entities" : qUnion([Q0, Q1, Q2]), "operationType" : NewBodyOperationType.ADD, "depth" : 2.54 * mm, "offsetDistance" : 25.4 * mm});
        }
        {
            var Q0;
            Q0=makeQuery(id+"F2.imprint","IMPRINT",FACE,{"disambiguationData":[TD([[makeQuery(id+"F2.imprint","IMPRINT",EDGE,{"derivedFrom":sQuery(id+"F2.wireOp",EDGE,"E3.0")}),1.0]])]});
            extrude(context, id + "F4", {"entities" : qUnion([Q0]), "operationType" : NewBodyOperationType.REMOVE, "oppositeDirection" : true, "depth" : 2.54 * mm, "offsetDistance" : 25.4 * mm});
        }
        {
            var Q0;
            Q0=makeQuery(id+"F2.imprint","IMPRINT",FACE,{"disambiguationData":[TD([[makeQuery(id+"F2.imprint","IMPRINT",EDGE,{"derivedFrom":sQuery(id+"F2.wireOp",EDGE,"E8.0")}),-1.0]])]});
            extrude(context, id + "F5", {"entities" : qUnion([Q0]), "operationType" : NewBodyOperationType.REMOVE, "oppositeDirection" : true, "depth" : 2.54 * mm, "offsetDistance" : 25.4 * mm});
        }
        {
            var Q0;
            {var subQ0=sQuery(id+"F2.wireOp",EDGE,"E13.2");var subQ1=sQuery(id+"F2.wireOp",EDGE,"E10.1");var subQ2=makeQuery(id+"F2.imprint","INTERSECT",VERTEX,{"derivedFrom":[subQ1,subQ0]});Q0=makeQuery(id+"F2.imprint","IMPRINT",FACE,{"disambiguationData":[TD([[makeQuery(id+"F2.imprint","IMPRINT",EDGE,{"disambiguationData":[TD([[subQ2,-1.0]])],"derivedFrom":subQ1}),1.0]])]});}
            var Q1;
            {var subQ0=sQuery(id+"F2.wireOp",EDGE,"E13.1");var subQ1=sQuery(id+"F2.wireOp",EDGE,"E10.0");var subQ2=makeQuery(id+"F2.imprint","INTERSECT",VERTEX,{"derivedFrom":[subQ1,subQ0]});Q1=makeQuery(id+"F2.imprint","IMPRINT",FACE,{"disambiguationData":[TD([[makeQuery(id+"F2.imprint","IMPRINT",EDGE,{"disambiguationData":[TD([[subQ2,-1.0]])],"derivedFrom":subQ1}),1.0]])]});}
            var Q2;
            {var subQ0=sQuery(id+"F2.wireOp",EDGE,"E13.0");var subQ1=sQuery(id+"F2.wireOp",EDGE,"E10.2");var subQ2=makeQuery(id+"F2.imprint","INTERSECT",VERTEX,{"derivedFrom":[subQ1,subQ0]});Q2=makeQuery(id+"F2.imprint","IMPRINT",FACE,{"disambiguationData":[TD([[makeQuery(id+"F2.imprint","IMPRINT",EDGE,{"disambiguationData":[TD([[subQ2,-1.0]])],"derivedFrom":subQ1}),1.0]])]});}
            extrude(context, id + "F6", {"entities" : qUnion([Q0, Q1, Q2]), "operationType" : NewBodyOperationType.REMOVE, "oppositeDirection" : true, "depth" : 2.54 * mm, "offsetDistance" : 25.4 * mm});
        }
        {
            var Q0;
            Q0=makeQuery(id+"F3.opExtrude","CAP_FACE",FACE,{"disambiguationData":[OSD([sQuery(id+"F0.wireOp",EDGE,"E0.0"),sQuery(id+"F0.wireOp",EDGE,"E0.1"),sQuery(id+"F0.wireOp",EDGE,"E0.2"),sQuery(id+"F0.wireOp",EDGE,"E0.3"),sQuery(id+"F0.wireOp",EDGE,"E0.4"),sQuery(id+"F0.wireOp",EDGE,"E1"),sQuery(id+"F0.wireOp",EDGE,"E2.sketch_text.stroke-0"),sQuery(id+"F0.wireOp",EDGE,"E2.sketch_text.stroke-1"),sQuery(id+"F0.wireOp",EDGE,"E2.sketch_text.stroke-2"),sQuery(id+"F0.wireOp",EDGE,"E2.sketch_text.stroke-3"),sQuery(id+"F0.wireOp",EDGE,"E2.sketch_text.stroke-4"),sQuery(id+"F0.wireOp",EDGE,"E2.sketch_text.stroke-5"),sQuery(id+"F0.wireOp",EDGE,"E2.sketch_text.stroke-6"),sQuery(id+"F0.wireOp",EDGE,"E2.sketch_text.stroke-7"),sQuery(id+"F0.wireOp",EDGE,"E2.sketch_text.stroke-8"),sQuery(id+"F0.wireOp",EDGE,"E2.sketch_text.stroke-9"),sQuery(id+"F0.wireOp",EDGE,"E2.sketch_text.stroke-10"),sQuery(id+"F0.wireOp",EDGE,"E2.sketch_text.stroke-11"),sQuery(id+"F0.wireOp",EDGE,"E2.sketch_text.stroke-12"),sQuery(id+"F0.wireOp",EDGE,"E2.sketch_text.stroke-13"),sQuery(id+"F0.wireOp",EDGE,"E2.sketch_text.stroke-14"),sQuery(id+"F0.wireOp",EDGE,"E2.sketch_text.stroke-15"),sQuery(id+"F0.wireOp",EDGE,"E2.sketch_text.stroke-16"),sQuery(id+"F0.wireOp",EDGE,"E2.sketch_text.stroke-17"),sQuery(id+"F0.wireOp",EDGE,"E2.sketch_text.stroke-18"),sQuery(id+"F0.wireOp",EDGE,"E2.sketch_text.stroke-19"),sQuery(id+"F0.wireOp",EDGE,"E2.sketch_text.stroke-20"),sQuery(id+"F0.wireOp",EDGE,"E2.sketch_text.stroke-21"),sQuery(id+"F0.wireOp",EDGE,"E2.sketch_text.stroke-22"),sQuery(id+"F0.wireOp",EDGE,"E2.sketch_text.stroke-23"),sQuery(id+"F0.wireOp",EDGE,"E2.sketch_text.stroke-24"),sQuery(id+"F0.wireOp",EDGE,"E2.sketch_text.stroke-25"),sQuery(id+"F0.wireOp",EDGE,"E2.sketch_text.stroke-26"),sQuery(id+"F0.wireOp",EDGE,"E2.sketch_text.stroke-27"),sQuery(id+"F0.wireOp",EDGE,"E2.sketch_text.stroke-28"),sQuery(id+"F0.wireOp",EDGE,"E2.sketch_text.stroke-29"),sQuery(id+"F0.wireOp",EDGE,"E2.sketch_text.stroke-30"),sQuery(id+"F0.wireOp",EDGE,"E2.sketch_text.stroke-31"),sQuery(id+"F0.wireOp",EDGE,"E2.sketch_text.stroke-32"),sQuery(id+"F0.wireOp",EDGE,"E2.sketch_text.stroke-33"),sQuery(id+"F0.wireOp",EDGE,"E2.sketch_text.stroke-34"),sQuery(id+"F0.wireOp",EDGE,"E2.sketch_text.stroke-35"),sQuery(id+"F0.wireOp",EDGE,"E2.sketch_text.stroke-36"),sQuery(id+"F0.wireOp",EDGE,"E2.sketch_text.stroke-37"),sQuery(id+"F0.wireOp",EDGE,"E2.sketch_text.stroke-38"),sQuery(id+"F0.wireOp",EDGE,"E2.sketch_text.stroke-39"),sQuery(id+"F0.wireOp",EDGE,"E2.sketch_text.stroke-40"),sQuery(id+"F0.wireOp",EDGE,"E2.sketch_text.stroke-41"),sQuery(id+"F0.wireOp",EDGE,"E2.sketch_text.stroke-42"),sQuery(id+"F0.wireOp",EDGE,"E2.sketch_text.stroke-43"),sQuery(id+"F0.wireOp",EDGE,"E2.sketch_text.stroke-44"),sQuery(id+"F0.wireOp",EDGE,"E2.sketch_text.stroke-45"),sQuery(id+"F0.wireOp",EDGE,"E2.sketch_text.stroke-46"),sQuery(id+"F0.wireOp",EDGE,"E2.sketch_text.stroke-47"),sQuery(id+"F0.wireOp",EDGE,"E2.sketch_text.stroke-48"),sQuery(id+"F0.wireOp",EDGE,"E2.sketch_text.stroke-49"),sQuery(id+"F0.wireOp",EDGE,"E2.sketch_text.stroke-50"),sQuery(id+"F0.wireOp",EDGE,"E2.sketch_text.stroke-51"),sQuery(id+"F0.wireOp",EDGE,"E2.sketch_text.stroke-52"),sQuery(id+"F0.wireOp",EDGE,"E2.sketch_text.stroke-53"),sQuery(id+"F0.wireOp",EDGE,"E2.sketch_text.stroke-54"),sQuery(id+"F0.wireOp",EDGE,"E2.sketch_text.stroke-55"),sQuery(id+"F0.wireOp",EDGE,"E2.sketch_text.stroke-56"),sQuery(id+"F0.wireOp",EDGE,"E2.sketch_text.stroke-57"),sQuery(id+"F0.wireOp",EDGE,"E2.sketch_text.stroke-58"),sQuery(id+"F0.wireOp",EDGE,"E2.sketch_text.stroke-59"),sQuery(id+"F0.wireOp",EDGE,"E2.sketch_text.stroke-60"),sQuery(id+"F0.wireOp",EDGE,"E2.sketch_text.stroke-61"),sQuery(id+"F0.wireOp",EDGE,"E2.sketch_text.stroke-62"),sQuery(id+"F0.wireOp",EDGE,"E2.sketch_text.stroke-63"),sQuery(id+"F0.wireOp",EDGE,"E2.sketch_text.stroke-64"),sQuery(id+"F0.wireOp",EDGE,"E2.sketch_text.stroke-65"),sQuery(id+"F0.wireOp",EDGE,"E2.sketch_text.stroke-66"),sQuery(id+"F0.wireOp",EDGE,"E2.sketch_text.stroke-67"),sQuery(id+"F0.wireOp",EDGE,"E2.sketch_text.stroke-68"),sQuery(id+"F0.wireOp",EDGE,"E2.sketch_text.stroke-69"),sQuery(id+"F0.wireOp",EDGE,"E2.sketch_text.stroke-70"),sQuery(id+"F0.wireOp",EDGE,"E2.sketch_text.stroke-71"),sQuery(id+"F0.wireOp",EDGE,"E2.sketch_text.stroke-72"),sQuery(id+"F0.wireOp",EDGE,"E2.sketch_text.stroke-73"),sQuery(id+"F0.wireOp",EDGE,"E2.sketch_text.stroke-74"),sQuery(id+"F0.wireOp",EDGE,"E2.sketch_text.stroke-75"),sQuery(id+"F0.wireOp",EDGE,"E2.sketch_text.stroke-76"),sQuery(id+"F0.wireOp",EDGE,"E2.sketch_text.stroke-77"),sQuery(id+"F0.wireOp",EDGE,"E2.sketch_text.stroke-78"),sQuery(id+"F0.wireOp",EDGE,"E2.sketch_text.stroke-79"),sQuery(id+"F0.wireOp",EDGE,"E2.sketch_text.stroke-80"),sQuery(id+"F0.wireOp",EDGE,"E2.sketch_text.stroke-81"),sQuery(id+"F0.wireOp",EDGE,"E2.sketch_text.stroke-82"),sQuery(id+"F0.wireOp",EDGE,"E2.sketch_text.stroke-83"),sQuery(id+"F0.wireOp",EDGE,"E2.sketch_text.stroke-84"),sQuery(id+"F0.wireOp",EDGE,"E2.sketch_text.stroke-85"),sQuery(id+"F0.wireOp",EDGE,"E2.sketch_text.stroke-86"),sQuery(id+"F0.wireOp",EDGE,"E2.sketch_text.stroke-87"),sQuery(id+"F0.wireOp",EDGE,"E2.sketch_text.stroke-88"),sQuery(id+"F0.wireOp",EDGE,"E2.sketch_text.stroke-89"),sQuery(id+"F0.wireOp",EDGE,"E2.sketch_text.stroke-90"),sQuery(id+"F0.wireOp",EDGE,"E2.sketch_text.stroke-91"),sQuery(id+"F0.wireOp",EDGE,"E2.sketch_text.stroke-92"),sQuery(id+"F0.wireOp",EDGE,"E2.sketch_text.stroke-93"),sQuery(id+"F0.wireOp",EDGE,"E2.sketch_text.stroke-94"),sQuery(id+"F0.wireOp",EDGE,"E2.sketch_text.stroke-95"),sQuery(id+"F0.wireOp",EDGE,"E2.sketch_text.stroke-96"),sQuery(id+"F0.wireOp",EDGE,"E2.sketch_text.stroke-97"),sQuery(id+"F0.wireOp",EDGE,"E2.sketch_text.stroke-98"),sQuery(id+"F0.wireOp",EDGE,"E2.sketch_text.stroke-99"),sQuery(id+"F0.wireOp",EDGE,"E2.sketch_text.stroke-100"),sQuery(id+"F0.wireOp",EDGE,"E2.sketch_text.stroke-101"),sQuery(id+"F0.wireOp",EDGE,"E2.sketch_text.stroke-102"),sQuery(id+"F0.wireOp",EDGE,"E2.sketch_text.stroke-103"),sQuery(id+"F0.wireOp",EDGE,"E2.sketch_text.stroke-104"),sQuery(id+"F0.wireOp",EDGE,"E2.sketch_text.stroke-105"),sQuery(id+"F0.wireOp",EDGE,"E2.sketch_text.stroke-106"),sQuery(id+"F0.wireOp",EDGE,"E2.sketch_text.stroke-107"),sQuery(id+"F0.wireOp",EDGE,"E2.sketch_text.stroke-108"),sQuery(id+"F0.wireOp",EDGE,"E2.sketch_text.stroke-109"),sQuery(id+"F0.wireOp",EDGE,"E2.sketch_text.stroke-110"),sQuery(id+"F0.wireOp",EDGE,"E2.sketch_text.stroke-111"),sQuery(id+"F0.wireOp",EDGE,"E2.sketch_text.stroke-112"),sQuery(id+"F0.wireOp",EDGE,"E2.sketch_text.stroke-113"),sQuery(id+"F0.wireOp",EDGE,"E2.sketch_text.stroke-114"),sQuery(id+"F0.wireOp",EDGE,"E2.sketch_text.stroke-115"),sQuery(id+"F0.wireOp",EDGE,"E2.sketch_text.stroke-116"),sQuery(id+"F0.wireOp",EDGE,"E2.sketch_text.stroke-117"),sQuery(id+"F0.wireOp",EDGE,"E2.sketch_text.stroke-118"),sQuery(id+"F0.wireOp",EDGE,"E2.sketch_text.stroke-119"),sQuery(id+"F0.wireOp",EDGE,"E2.sketch_text.stroke-120"),sQuery(id+"F0.wireOp",EDGE,"E2.sketch_text.stroke-121"),sQuery(id+"F0.wireOp",EDGE,"E2.sketch_text.stroke-122"),sQuery(id+"F0.wireOp",EDGE,"E2.sketch_text.stroke-123"),sQuery(id+"F0.wireOp",EDGE,"E2.sketch_text.stroke-124"),sQuery(id+"F0.wireOp",EDGE,"E2.sketch_text.stroke-125"),sQuery(id+"F0.wireOp",EDGE,"E2.sketch_text.stroke-126"),sQuery(id+"F0.wireOp",EDGE,"E2.sketch_text.stroke-127"),sQuery(id+"F0.wireOp",EDGE,"E2.sketch_text.stroke-128"),sQuery(id+"F0.wireOp",EDGE,"E2.sketch_text.stroke-129"),sQuery(id+"F0.wireOp",EDGE,"E2.sketch_text.stroke-130"),sQuery(id+"F0.wireOp",EDGE,"E2.sketch_text.stroke-131"),sQuery(id+"F0.wireOp",EDGE,"E2.sketch_text.stroke-132"),sQuery(id+"F0.wireOp",EDGE,"E2.sketch_text.stroke-133"),sQuery(id+"F0.wireOp",EDGE,"E2.sketch_text.stroke-134"),sQuery(id+"F0.wireOp",EDGE,"E2.sketch_text.stroke-135"),sQuery(id+"F0.wireOp",EDGE,"E2.sketch_text.stroke-136"),sQuery(id+"F0.wireOp",EDGE,"E2.sketch_text.stroke-137"),sQuery(id+"F0.wireOp",EDGE,"E2.sketch_text.stroke-138"),sQuery(id+"F0.wireOp",EDGE,"E2.sketch_text.stroke-139"),sQuery(id+"F0.wireOp",EDGE,"E2.sketch_text.stroke-140"),sQuery(id+"F0.wireOp",EDGE,"E2.sketch_text.stroke-141"),sQuery(id+"F0.wireOp",EDGE,"E2.sketch_text.stroke-142"),sQuery(id+"F0.wireOp",EDGE,"E2.sketch_text.stroke-143"),sQuery(id+"F0.wireOp",EDGE,"E2.sketch_text.stroke-144"),sQuery(id+"F0.wireOp",EDGE,"E2.sketch_text.stroke-145"),sQuery(id+"F0.wireOp",EDGE,"E2.sketch_text.stroke-146"),sQuery(id+"F0.wireOp",EDGE,"E2.sketch_text.stroke-147"),sQuery(id+"F0.wireOp",EDGE,"E2.sketch_text.stroke-148"),sQuery(id+"F0.wireOp",EDGE,"E2.sketch_text.stroke-149"),sQuery(id+"F0.wireOp",EDGE,"E2.sketch_text.stroke-150"),sQuery(id+"F0.wireOp",EDGE,"E2.sketch_text.stroke-151"),sQuery(id+"F0.wireOp",EDGE,"E2.sketch_text.stroke-152"),sQuery(id+"F0.wireOp",EDGE,"E2.sketch_text.stroke-153"),sQuery(id+"F0.wireOp",EDGE,"E2.sketch_text.stroke-154"),sQuery(id+"F0.wireOp",EDGE,"E2.sketch_text.stroke-155"),sQuery(id+"F0.wireOp",EDGE,"E2.sketch_text.stroke-156"),sQuery(id+"F0.wireOp",EDGE,"E2.sketch_text.stroke-157"),sQuery(id+"F0.wireOp",EDGE,"E2.sketch_text.stroke-158"),sQuery(id+"F0.wireOp",EDGE,"E2.sketch_text.stroke-159"),sQuery(id+"F0.wireOp",EDGE,"E2.sketch_text.stroke-160"),sQuery(id+"F0.wireOp",EDGE,"E2.sketch_text.stroke-161"),sQuery(id+"F0.wireOp",EDGE,"E2.sketch_text.stroke-162"),sQuery(id+"F0.wireOp",EDGE,"E2.sketch_text.stroke-163"),sQuery(id+"F0.wireOp",EDGE,"E2.sketch_text.stroke-164"),sQuery(id+"F0.wireOp",EDGE,"E2.sketch_text.stroke-165"),sQuery(id+"F0.wireOp",EDGE,"E2.sketch_text.stroke-166"),sQuery(id+"F0.wireOp",EDGE,"E2.sketch_text.stroke-167"),sQuery(id+"F0.wireOp",EDGE,"E2.sketch_text.stroke-168"),sQuery(id+"F0.wireOp",EDGE,"E2.sketch_text.stroke-169"),sQuery(id+"F0.wireOp",EDGE,"E2.sketch_text.stroke-170"),sQuery(id+"F0.wireOp",EDGE,"E2.sketch_text.stroke-171"),sQuery(id+"F0.wireOp",EDGE,"E2.sketch_text.stroke-172"),sQuery(id+"F0.wireOp",EDGE,"E2.sketch_text.stroke-173"),sQuery(id+"F0.wireOp",EDGE,"E2.sketch_text.stroke-174"),sQuery(id+"F0.wireOp",EDGE,"E2.sketch_text.stroke-175"),sQuery(id+"F0.wireOp",EDGE,"E2.sketch_text.stroke-176"),sQuery(id+"F0.wireOp",EDGE,"E2.sketch_text.stroke-177"),sQuery(id+"F0.wireOp",EDGE,"E2.sketch_text.stroke-178"),sQuery(id+"F0.wireOp",EDGE,"E2.sketch_text.stroke-179"),sQuery(id+"F0.wireOp",EDGE,"E2.sketch_text.stroke-180"),sQuery(id+"F0.wireOp",EDGE,"E2.sketch_text.stroke-181"),sQuery(id+"F0.wireOp",EDGE,"E2.sketch_text.stroke-182"),sQuery(id+"F0.wireOp",EDGE,"E2.sketch_text.stroke-183"),sQuery(id+"F0.wireOp",EDGE,"E2.sketch_text.stroke-184"),sQuery(id+"F0.wireOp",EDGE,"E2.sketch_text.stroke-185"),sQuery(id+"F0.wireOp",EDGE,"E2.sketch_text.stroke-186"),sQuery(id+"F0.wireOp",EDGE,"E2.sketch_text.stroke-187"),sQuery(id+"F0.wireOp",EDGE,"E2.sketch_text.stroke-188"),sQuery(id+"F0.wireOp",EDGE,"E2.sketch_text.stroke-189"),sQuery(id+"F0.wireOp",EDGE,"E2.sketch_text.stroke-190"),sQuery(id+"F0.wireOp",EDGE,"E2.sketch_text.stroke-191"),sQuery(id+"F0.wireOp",EDGE,"E2.sketch_text.stroke-192"),sQuery(id+"F0.wireOp",EDGE,"E2.sketch_text.stroke-193"),sQuery(id+"F0.wireOp",EDGE,"E2.sketch_text.stroke-194"),sQuery(id+"F0.wireOp",EDGE,"E2.sketch_text.stroke-195"),sQuery(id+"F0.wireOp",EDGE,"E2.sketch_text.stroke-196"),sQuery(id+"F0.wireOp",EDGE,"E2.sketch_text.stroke-197"),sQuery(id+"F0.wireOp",EDGE,"E2.sketch_text.stroke-198"),sQuery(id+"F0.wireOp",EDGE,"E2.sketch_text.stroke-199"),sQuery(id+"F0.wireOp",EDGE,"E2.sketch_text.stroke-200"),sQuery(id+"F0.wireOp",EDGE,"E2.sketch_text.stroke-201"),sQuery(id+"F0.wireOp",EDGE,"E2.sketch_text.stroke-202"),sQuery(id+"F0.wireOp",EDGE,"E2.sketch_text.stroke-203"),sQuery(id+"F0.wireOp",EDGE,"E2.sketch_text.stroke-204"),sQuery(id+"F0.wireOp",EDGE,"E2.sketch_text.stroke-205"),sQuery(id+"F0.wireOp",EDGE,"E2.sketch_text.stroke-206"),sQuery(id+"F0.wireOp",EDGE,"E2.sketch_text.stroke-207"),sQuery(id+"F0.wireOp",EDGE,"E2.sketch_text.stroke-208"),sQuery(id+"F0.wireOp",EDGE,"E2.sketch_text.stroke-209"),sQuery(id+"F0.wireOp",EDGE,"E2.sketch_text.stroke-210"),sQuery(id+"F0.wireOp",EDGE,"E2.sketch_text.stroke-211"),sQuery(id+"F0.wireOp",EDGE,"E2.sketch_text.stroke-212"),sQuery(id+"F0.wireOp",EDGE,"E2.sketch_text.stroke-213"),sQuery(id+"F0.wireOp",EDGE,"E2.sketch_text.stroke-214"),sQuery(id+"F0.wireOp",EDGE,"E2.sketch_text.stroke-215"),sQuery(id+"F0.wireOp",EDGE,"E2.sketch_text.stroke-216"),sQuery(id+"F0.wireOp",EDGE,"E2.sketch_text.stroke-217"),sQuery(id+"F0.wireOp",EDGE,"E2.sketch_text.stroke-218"),sQuery(id+"F0.wireOp",EDGE,"E2.sketch_text.stroke-219"),sQuery(id+"F0.wireOp",EDGE,"E2.sketch_text.stroke-220"),sQuery(id+"F0.wireOp",EDGE,"E2.sketch_text.stroke-221"),sQuery(id+"F0.wireOp",EDGE,"E2.sketch_text.stroke-222"),sQuery(id+"F0.wireOp",EDGE,"E2.sketch_text.stroke-223"),sQuery(id+"F0.wireOp",EDGE,"E2.sketch_text.stroke-224"),sQuery(id+"F0.wireOp",EDGE,"E2.sketch_text.stroke-225"),sQuery(id+"F0.wireOp",EDGE,"E2.sketch_text.stroke-226"),sQuery(id+"F0.wireOp",EDGE,"E2.sketch_text.stroke-227"),sQuery(id+"F0.wireOp",EDGE,"E2.sketch_text.stroke-228"),sQuery(id+"F0.wireOp",EDGE,"E2.sketch_text.stroke-229"),sQuery(id+"F0.wireOp",EDGE,"E2.sketch_text.stroke-230"),sQuery(id+"F0.wireOp",EDGE,"E2.sketch_text.stroke-231"),sQuery(id+"F0.wireOp",EDGE,"E2.sketch_text.stroke-232"),sQuery(id+"F0.wireOp",EDGE,"E2.sketch_text.stroke-233"),sQuery(id+"F0.wireOp",EDGE,"E2.sketch_text.stroke-234"),sQuery(id+"F0.wireOp",EDGE,"E2.sketch_text.stroke-235"),sQuery(id+"F2.wireOp",EDGE,"E5.0"),sQuery(id+"F2.wireOp",EDGE,"E5.1"),sQuery(id+"F2.wireOp",EDGE,"E5.2"),sQuery(id+"F2.wireOp",EDGE,"E5.3"),sQuery(id+"F2.wireOp",EDGE,"E5.4"),sQuery(id+"F2.wireOp",EDGE,"E5.5"),sQuery(id+"F2.wireOp",EDGE,"E5.6"),sQuery(id+"F2.wireOp",EDGE,"E5.7"),sQuery(id+"F2.wireOp",EDGE,"E5.8"),sQuery(id+"F2.wireOp",EDGE,"E5.9"),sQuery(id+"F2.wireOp",EDGE,"E5.10"),sQuery(id+"F2.wireOp",EDGE,"E5.11"),sQuery(id+"F2.wireOp",EDGE,"E5.12"),sQuery(id+"F2.wireOp",EDGE,"E5.13"),sQuery(id+"F2.wireOp",EDGE,"E5.14"),sQuery(id+"F2.wireOp",EDGE,"E5.15"),sQuery(id+"F2.wireOp",EDGE,"E5.16"),sQuery(id+"F2.wireOp",EDGE,"E5.17"),sQuery(id+"F2.wireOp",EDGE,"E5.18"),sQuery(id+"F2.wireOp",EDGE,"E5.19"),sQuery(id+"F2.wireOp",EDGE,"E5.20"),sQuery(id+"F2.wireOp",EDGE,"E5.21"),sQuery(id+"F2.wireOp",EDGE,"E5.22"),sQuery(id+"F2.wireOp",EDGE,"E5.23"),sQuery(id+"F2.wireOp",EDGE,"E5.24"),sQuery(id+"F2.wireOp",EDGE,"E5.25"),sQuery(id+"F2.wireOp",EDGE,"E5.26"),sQuery(id+"F2.wireOp",EDGE,"E5.27"),sQuery(id+"F2.wireOp",EDGE,"E5.28"),sQuery(id+"F2.wireOp",EDGE,"E5.29"),sQuery(id+"F2.wireOp",EDGE,"E5.30"),sQuery(id+"F2.wireOp",EDGE,"E5.31"),sQuery(id+"F2.wireOp",EDGE,"E5.32"),sQuery(id+"F2.wireOp",EDGE,"E5.33"),sQuery(id+"F2.wireOp",EDGE,"E5.34"),sQuery(id+"F2.wireOp",EDGE,"E5.35"),sQuery(id+"F2.wireOp",EDGE,"E5.36"),sQuery(id+"F2.wireOp",EDGE,"E5.37"),sQuery(id+"F2.wireOp",EDGE,"E5.38"),sQuery(id+"F2.wireOp",EDGE,"E5.39"),sQuery(id+"F2.wireOp",EDGE,"E5.40"),sQuery(id+"F2.wireOp",EDGE,"E5.41"),sQuery(id+"F2.wireOp",EDGE,"E5.42"),sQuery(id+"F2.wireOp",EDGE,"E5.43"),sQuery(id+"F2.wireOp",EDGE,"E5.44"),sQuery(id+"F2.wireOp",EDGE,"E5.45"),sQuery(id+"F2.wireOp",EDGE,"E5.46"),sQuery(id+"F2.wireOp",EDGE,"E5.47"),sQuery(id+"F2.wireOp",EDGE,"E5.48"),sQuery(id+"F2.wireOp",EDGE,"E5.49"),sQuery(id+"F2.wireOp",EDGE,"E9.0"),sQuery(id+"F2.wireOp",EDGE,"E9.1"),sQuery(id+"F2.wireOp",EDGE,"E9.2"),sQuery(id+"F2.wireOp",EDGE,"E9.3"),sQuery(id+"F2.wireOp",EDGE,"E9.4"),sQuery(id+"F2.wireOp",EDGE,"E9.5"),sQuery(id+"F2.wireOp",EDGE,"E14.0"),sQuery(id+"F2.wireOp",EDGE,"E14.1"),sQuery(id+"F2.wireOp",EDGE,"E14.2"),sQuery(id+"F2.wireOp",EDGE,"E14.3"),sQuery(id+"F2.wireOp",EDGE,"E14.4"),sQuery(id+"F2.wireOp",EDGE,"E14.5")])],"isStart":false});
            var sketch = newSketch(context, id + "F7", { "sketchPlane" : qUnion([Q0])});
            skFitSpline(sketch, "E16", {"points": [v(-17.33, -16) * mm, v(-15.98, -19.74) * mm, v(-15.33, -23.08) * mm, v(-15.98, -25.33) * mm, v(-15.33, -25.38) * mm, v(-14.42, -23.12) * mm, v(-14.5, -21.38) * mm, v(-14.6, -21.17) * mm, v(-13.33, -22) * mm, v(-11.77, -21.34) * mm, v(-12.86, -20.34) * mm, v(-14.42, -20.39) * mm, v(-14.98, -19.08) * mm, v(-15.85, -16.78) * mm, v(-16.5, -16.4) * mm, v(-17.33, -16) * mm]});
            skPoint(sketch, "E17.6.internal.snap0", {"position": v(17.37, -1.58) * mm});
            skPoint(sketch, "E17.9.internal.snap0", {"position": v(17.37, -1.58) * mm});
            skPoint(sketch, "E17.11.internal.snap0", {"position": v(17.37, -1.58) * mm});
            skPoint(sketch, "E17.12.internal.snap0", {"position": v(17.37, -1.58) * mm});
            skFitSpline(sketch, "E17", {"points": [v(20.43, -18.32) * mm, v(20.55, -19.56) * mm, v(19.02, -17.53) * mm, v(18.74, -16.83) * mm, v(18.6, -18.09) * mm, v(17.6, -18.35) * mm, v(17.37, -17.52) * mm, v(17.7, -16.87) * mm, v(18.3, -16.61) * mm, v(17.37, -15.48) * mm, v(16.65, -13.23) * mm, v(17.37, -13.14) * mm, v(17.37, -13.88) * mm, v(18.74, -15.91) * mm, v(20.02, -17.86) * mm, v(20.43, -18.32) * mm]});
            skFitSpline(sketch, "E18", {"points": [v(17.82, 5.17) * mm, v(18.85, 5.94) * mm, v(19.69, 5.17) * mm, v(21.77, 4.39) * mm, v(24.85, 4) * mm, v(28.23, 4.9) * mm, v(27.97, 4.13) * mm, v(26.37, 3.52) * mm, v(24.98, 3.09) * mm, v(23.5, 3.09) * mm, v(22.38, 3.26) * mm, v(20.53, 3.74) * mm, v(20.9, 2.73) * mm, v(20.16, 1.61) * mm, v(19.38, 2.73) * mm, v(19.82, 3.48) * mm, v(19.9, 3.87) * mm, v(18.43, 4.7) * mm, v(17.82, 5.17) * mm]});
            skSolve(sketch);
        }
        {
            var Q0;
            Q0=makeQuery(id+"F7.imprint","IMPRINT",FACE,{"disambiguationData":[TD([[makeQuery(id+"F7.imprint","IMPRINT",EDGE,{"derivedFrom":sQuery(id+"F7.wireOp",EDGE,"E18")}),-1.0]])]});
            var Q1;
            Q1=makeQuery(id+"F7.imprint","IMPRINT",FACE,{"disambiguationData":[TD([[makeQuery(id+"F7.imprint","IMPRINT",EDGE,{"derivedFrom":sQuery(id+"F7.wireOp",EDGE,"E17")}),-1.0]])]});
            var Q2;
            Q2=makeQuery(id+"F7.imprint","IMPRINT",FACE,{"disambiguationData":[TD([[makeQuery(id+"F7.imprint","IMPRINT",EDGE,{"derivedFrom":sQuery(id+"F7.wireOp",EDGE,"E16")}),1.0]])]});
            var Q3;
            Q3=sQuery(id+"F7.wireOp",EDGE,"E17");
            var Q4;
            Q4=sQuery(id+"F7.wireOp",EDGE,"E16");
            var Q5;
            Q5=sQuery(id+"F7.wireOp",EDGE,"E18");
            var Q6;
            Q6=sQuery(id+"F7.wireOp",EDGE,"E16");
            var Q7;
            Q7=sQuery(id+"F7.wireOp",EDGE,"E18");
            extrude(context, id + "F8", {"entities" : qUnion([Q0, Q1, Q2]), "operationType" : NewBodyOperationType.ADD, "surfaceOperationType" : NewSurfaceOperationType.ADD, "surfaceEntities" : qUnion([Q3, Q4, Q5, Q6, Q7]), "depth" : 1.27 * mm, "offsetDistance" : 25.4 * mm});
        }
    });
